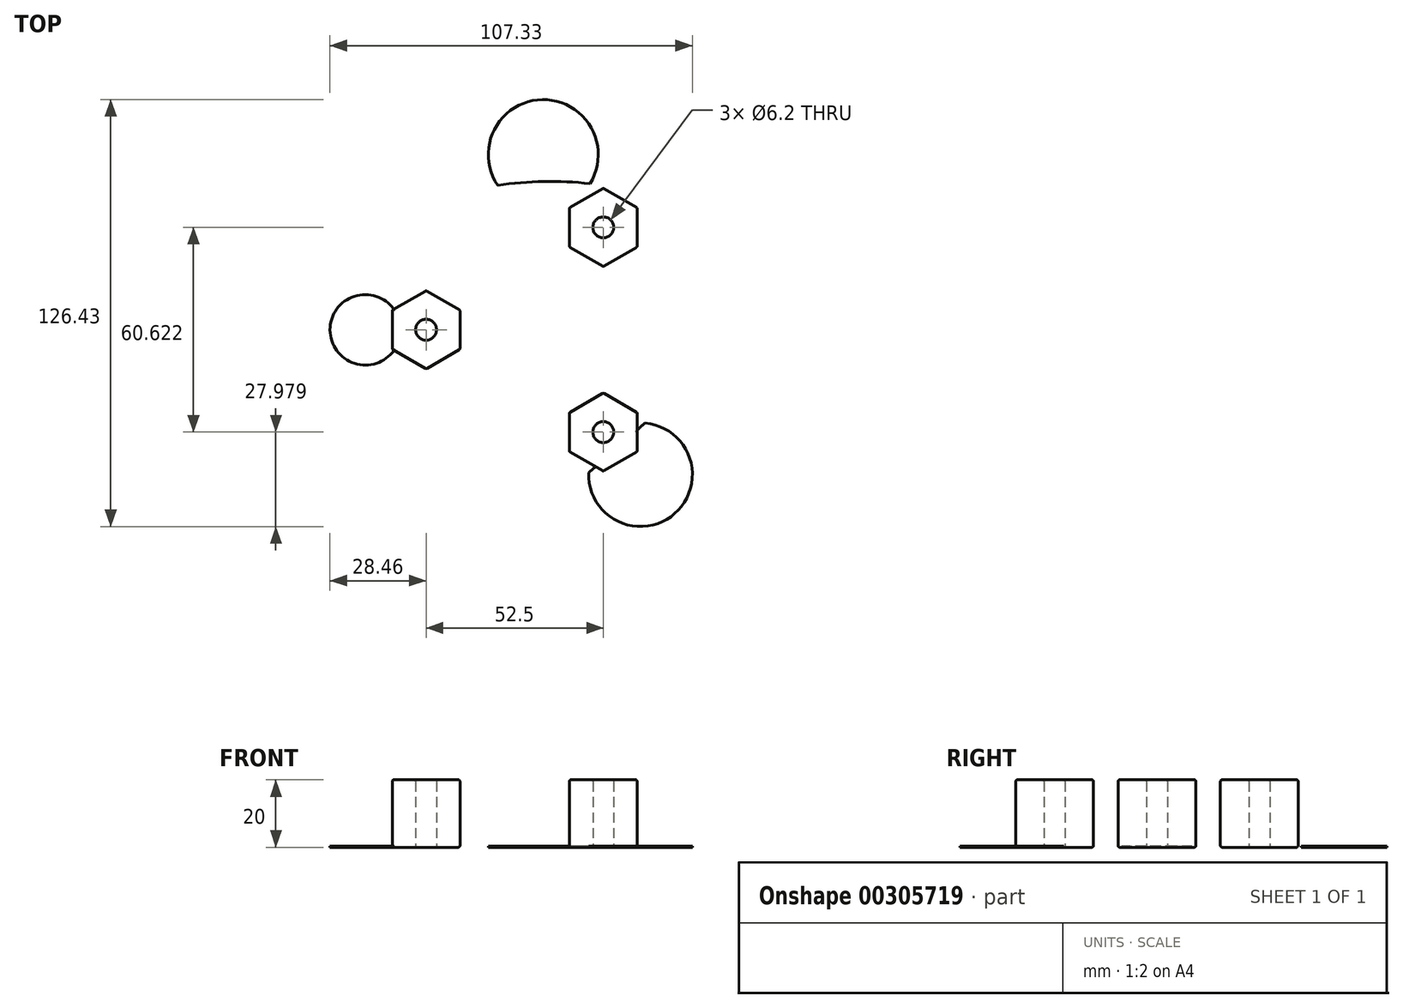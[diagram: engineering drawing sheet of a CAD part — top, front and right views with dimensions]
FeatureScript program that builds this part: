
annotation { "Feature Type Name" : "Feature", "Feature Type Description" : "" }
export const myFeature = defineFeature(function(context is Context, id is Id, definition is map)
    precondition{}
    {
        {
            var Q0;
            Q0=qCreatedBy(makeId("Top.planeOp"),FACE);
            var sketch = newSketch(context, id + "F0", { "sketchPlane" : qUnion([Q0])});
            skCircle(sketch, "E0.cCircle", {"center": v(0, 0) * mm, "radius": 52 * mm, "construction": true});
            skLineSegment(sketch, "E0.0", {"start": v(15, 43.34) * mm, "end": v(27.53, 36.1) * mm});
            skLineSegment(sketch, "E0.2", {"start": v(27.53, -36.1) * mm, "end": v(15, -43.34) * mm});
            skLineSegment(sketch, "E0.4", {"start": v(-45.03, -5.8) * mm, "end": v(-45.03, 5.8) * mm});
            skCircle(sketch, "E1", {"center": v(0, 38) * mm, "radius": 2.1 * mm});
            skCircle(sketch, "E2", {"center": v(0, -38) * mm, "radius": 2.1 * mm});
            skCircle(sketch, "E3.cCircle", {"center": v(0, 0) * mm, "radius": 35 * mm, "construction": true});
            skLineSegment(sketch, "E3.0", {"start": v(-35, 0) * mm, "end": v(-32.32, 1.55) * mm});
            skLineSegment(sketch, "E3.1", {"start": v(17.5, 30.31) * mm, "end": v(17.5, 27.21) * mm});
            skLineSegment(sketch, "E3.2", {"start": v(17.5, -30.31) * mm, "end": v(14.82, -28.76) * mm});
            skCircle(sketch, "E4", {"center": v(17.5, 30.31) * mm, "radius": 3.1 * mm});
            skCircle(sketch, "E5", {"center": v(17.5, -30.31) * mm, "radius": 3.1 * mm});
            skCircle(sketch, "E6", {"center": v(-35, 0) * mm, "radius": 3.1 * mm});
            skLineSegment(sketch, "E7.trimOffspring", {"start": v(14.82, 28.76) * mm, "end": v(17.5, 30.31) * mm});
            skLineSegment(sketch, "E8.trimOffspring", {"start": v(-32.32, -1.55) * mm, "end": v(-35, 0) * mm});
            skLineSegment(sketch, "E9.trimOffspring", {"start": v(17.5, -27.21) * mm, "end": v(17.5, -30.31) * mm});
            skCircle(sketch, "E10.cCircle", {"center": v(17.5, 30.31) * mm, "radius": 5.05 * mm, "construction": true});
            skLineSegment(sketch, "E10.0", {"start": v(17.5, 36.14) * mm, "end": v(22.55, 33.23) * mm});
            skLineSegment(sketch, "E10.1", {"start": v(22.55, 33.23) * mm, "end": v(22.55, 27.4) * mm});
            skLineSegment(sketch, "E10.2", {"start": v(22.55, 27.4) * mm, "end": v(17.5, 24.48) * mm});
            skLineSegment(sketch, "E10.3", {"start": v(17.5, 24.48) * mm, "end": v(12.45, 27.4) * mm});
            skLineSegment(sketch, "E10.4", {"start": v(12.45, 27.4) * mm, "end": v(12.45, 33.23) * mm});
            skLineSegment(sketch, "E10.5", {"start": v(12.45, 33.23) * mm, "end": v(17.5, 36.14) * mm});
            skCircle(sketch, "E11.cCircle", {"center": v(-35, 0) * mm, "radius": 5.05 * mm, "construction": true});
            skLineSegment(sketch, "E11.0", {"start": v(-29.95, 2.92) * mm, "end": v(-29.95, -2.92) * mm});
            skLineSegment(sketch, "E11.1", {"start": v(-29.95, -2.92) * mm, "end": v(-35, -5.83) * mm});
            skLineSegment(sketch, "E11.2", {"start": v(-35, -5.83) * mm, "end": v(-40.05, -2.92) * mm});
            skLineSegment(sketch, "E11.3", {"start": v(-40.05, -2.92) * mm, "end": v(-40.05, 2.92) * mm});
            skLineSegment(sketch, "E11.4", {"start": v(-40.05, 2.92) * mm, "end": v(-35, 5.83) * mm});
            skLineSegment(sketch, "E11.5", {"start": v(-35, 5.83) * mm, "end": v(-29.95, 2.92) * mm});
            skPoint(sketch, "E11.0.midPoint", {"position": v(-29.95, 0) * mm});
            skCircle(sketch, "E12.cCircle", {"center": v(17.5, -30.31) * mm, "radius": 5.05 * mm, "construction": true});
            skLineSegment(sketch, "E12.0", {"start": v(22.55, -33.23) * mm, "end": v(17.5, -36.14) * mm});
            skLineSegment(sketch, "E12.1", {"start": v(17.5, -36.14) * mm, "end": v(12.45, -33.23) * mm});
            skLineSegment(sketch, "E12.2", {"start": v(12.45, -33.23) * mm, "end": v(12.45, -27.4) * mm});
            skLineSegment(sketch, "E12.3", {"start": v(12.45, -27.4) * mm, "end": v(17.5, -24.48) * mm});
            skLineSegment(sketch, "E12.4", {"start": v(17.5, -24.48) * mm, "end": v(22.55, -27.4) * mm});
            skLineSegment(sketch, "E12.5", {"start": v(22.55, -27.4) * mm, "end": v(22.55, -33.23) * mm});
            skPoint(sketch, "E12.0.midPoint", {"position": v(20.02, -34.68) * mm});
            skCircle(sketch, "E13.cCircle", {"center": v(17.5, 30.31) * mm, "radius": 10.03 * mm, "construction": true});
            skLineSegment(sketch, "E13.0", {"start": v(17.5, 41.9) * mm, "end": v(27.53, 36.1) * mm});
            skLineSegment(sketch, "E13.1", {"start": v(27.53, 36.1) * mm, "end": v(27.53, 24.52) * mm});
            skLineSegment(sketch, "E13.2", {"start": v(27.53, 24.52) * mm, "end": v(17.5, 18.73) * mm});
            skLineSegment(sketch, "E13.3", {"start": v(17.5, 18.73) * mm, "end": v(7.47, 24.52) * mm});
            skLineSegment(sketch, "E13.4", {"start": v(7.47, 24.52) * mm, "end": v(7.47, 36.1) * mm});
            skLineSegment(sketch, "E13.5", {"start": v(7.47, 36.1) * mm, "end": v(17.5, 41.9) * mm});
            skCircle(sketch, "E14.cCircle", {"center": v(-35, 0) * mm, "radius": 10.03 * mm, "construction": true});
            skLineSegment(sketch, "E14.1", {"start": v(-45.03, 5.8) * mm, "end": v(-35, 11.59) * mm});
            skLineSegment(sketch, "E14.2", {"start": v(-35, 11.59) * mm, "end": v(-24.97, 5.8) * mm});
            skLineSegment(sketch, "E14.3", {"start": v(-24.97, 5.8) * mm, "end": v(-24.97, -5.8) * mm});
            skLineSegment(sketch, "E14.4", {"start": v(-24.97, -5.8) * mm, "end": v(-35, -11.59) * mm});
            skLineSegment(sketch, "E14.5", {"start": v(-35, -11.59) * mm, "end": v(-45.03, -5.8) * mm});
            skPoint(sketch, "E14.0.midPoint", {"position": v(-45.03, 0) * mm});
            skCircle(sketch, "E15.cCircle", {"center": v(17.5, -30.31) * mm, "radius": 10.03 * mm, "construction": true});
            skLineSegment(sketch, "E15.0", {"start": v(27.53, -36.1) * mm, "end": v(17.5, -41.9) * mm});
            skLineSegment(sketch, "E15.1", {"start": v(17.5, -41.9) * mm, "end": v(7.47, -36.1) * mm});
            skLineSegment(sketch, "E15.2", {"start": v(7.47, -36.1) * mm, "end": v(7.47, -24.52) * mm});
            skLineSegment(sketch, "E15.3", {"start": v(7.47, -24.52) * mm, "end": v(17.5, -18.73) * mm});
            skLineSegment(sketch, "E15.4", {"start": v(17.5, -18.73) * mm, "end": v(27.53, -24.52) * mm});
            skLineSegment(sketch, "E15.5", {"start": v(27.53, -24.52) * mm, "end": v(27.53, -36.1) * mm});
            skPoint(sketch, "E16.endSnap0", {"position": v(45.03, 0) * mm});
            skLineSegment(sketch, "E17", {"start": v(29.5, 10.5) * mm, "end": v(-11.5, 10.5) * mm});
            skLineSegment(sketch, "E18", {"start": v(-11.5, -10.5) * mm, "end": v(29.5, -10.5) * mm});
            skArc(sketch, "E19", {"start": v(-13.17, 3.97) * mm, "mid": v(-15, 7.1) * mm, "end": v(-16.83, 3.97) * mm});
            skArc(sketch, "E20", {"start": v(-16.83, -3.97) * mm, "mid": v(-15, -7.1) * mm, "end": v(-13.17, -3.97) * mm});
            skArc(sketch, "E21", {"start": v(34.83, 3.97) * mm, "mid": v(33.03, 7.1) * mm, "end": v(31.14, 4.02) * mm});
            skArc(sketch, "E22", {"start": v(34.3, -6.97) * mm, "mid": v(35.3, -5.55) * mm, "end": v(35.05, -3.84) * mm});
            skLineSegment(sketch, "E23", {"start": v(9, -10.5) * mm, "end": v(9, 10.5) * mm});
            skPoint(sketch, "E24.visualSharp", {"position": v(31.35, -3.32) * mm});
            skPoint(sketch, "E25.endSnap0", {"position": v(-11.5, 0) * mm});
            skLineSegment(sketch, "E26", {"start": v(-17.5, 0) * mm, "end": v(-17.5, 3.19) * mm});
            skLineSegment(sketch, "E27", {"start": v(-17.19, 3.5) * mm, "end": v(-17.1, 3.5) * mm});
            skLineSegment(sketch, "E28", {"start": v(-12.31, -3.5) * mm, "end": v(-12.9, -3.5) * mm});
            skLineSegment(sketch, "E29", {"start": v(-17.5, -3.19) * mm, "end": v(-17.5, 0) * mm});
            skLineSegment(sketch, "E30.trimOffspring", {"start": v(-12.9, 3.5) * mm, "end": v(-12.31, 3.5) * mm});
            skLineSegment(sketch, "E31.trimOffspring", {"start": v(-17.1, -3.5) * mm, "end": v(-17.19, -3.5) * mm});
            skPoint(sketch, "E25.start.orphan", {"position": v(-11.5, 0) * mm});
            skPoint(sketch, "E32.visualSharp", {"position": v(-13.53, 3.5) * mm});
            skArc(sketch, "E32.filletArc", {"start": v(-13.17, 3.97) * mm, "mid": v(-13.17, 3.65) * mm, "end": v(-12.9, 3.5) * mm});
            skPoint(sketch, "E33.visualSharp", {"position": v(-16.47, 3.5) * mm});
            skArc(sketch, "E33.filletArc", {"start": v(-17.1, 3.5) * mm, "mid": v(-16.83, 3.65) * mm, "end": v(-16.83, 3.97) * mm});
            skPoint(sketch, "E34.visualSharp", {"position": v(-17.5, 3.5) * mm});
            skArc(sketch, "E34.filletArc", {"start": v(-17.19, 3.5) * mm, "mid": v(-17.4, 3.4) * mm, "end": v(-17.5, 3.19) * mm});
            skPoint(sketch, "E35.visualSharp", {"position": v(-16.47, -3.5) * mm});
            skArc(sketch, "E35.filletArc", {"start": v(-16.83, -3.97) * mm, "mid": v(-16.83, -3.65) * mm, "end": v(-17.1, -3.5) * mm});
            skPoint(sketch, "E36.visualSharp", {"position": v(-17.5, -3.5) * mm});
            skArc(sketch, "E36.filletArc", {"start": v(-17.5, -3.19) * mm, "mid": v(-17.4, -3.4) * mm, "end": v(-17.19, -3.5) * mm});
            skPoint(sketch, "E37.visualSharp", {"position": v(-13.53, -3.5) * mm});
            skArc(sketch, "E37.filletArc", {"start": v(-12.9, -3.5) * mm, "mid": v(-13.17, -3.65) * mm, "end": v(-13.17, -3.97) * mm});
            skPoint(sketch, "E38.visualSharp", {"position": v(-11.5, -3.5) * mm});
            skPoint(sketch, "E39.visualSharp", {"position": v(-11.5, 3.5) * mm});
            skArc(sketch, "E40", {"start": v(31.14, 4.02) * mm, "mid": v(32.97, 2.9) * mm, "end": v(34.83, 3.97) * mm});
            skArc(sketch, "E41", {"start": v(35.05, -3.84) * mm, "mid": v(30.7, -4.45) * mm, "end": v(34.3, -6.97) * mm});
            skLineSegment(sketch, "E42.bottom", {"start": v(29.5, 10.5) * mm, "end": v(30, 10.5) * mm});
            skLineSegment(sketch, "E42.top", {"start": v(29.5, -10.5) * mm, "end": v(30, -10.5) * mm});
            skLineSegment(sketch, "E42.right", {"start": v(30, 10.5) * mm, "end": v(30, -10.5) * mm});
            skLineSegment(sketch, "E43.bottom", {"start": v(-11.5, 10.5) * mm, "end": v(-12, 10.5) * mm});
            skLineSegment(sketch, "E43.right", {"start": v(-12, 10.5) * mm, "end": v(-12, 3.81) * mm});
            skLineSegment(sketch, "E44.bottom", {"start": v(-11.5, -10.5) * mm, "end": v(-12, -10.5) * mm});
            skLineSegment(sketch, "E44.right", {"start": v(-12, -10.5) * mm, "end": v(-12, -3.81) * mm});
            skPoint(sketch, "E45.visualSharp", {"position": v(-12, -3.5) * mm});
            skArc(sketch, "E45.filletArc", {"start": v(-12, -3.81) * mm, "mid": v(-12.1, -3.6) * mm, "end": v(-12.31, -3.5) * mm});
            skPoint(sketch, "E46.visualSharp", {"position": v(-12, 3.5) * mm});
            skArc(sketch, "E46.filletArc", {"start": v(-12.31, 3.5) * mm, "mid": v(-12.1, 3.6) * mm, "end": v(-12, 3.81) * mm});
            skPoint(sketch, "E47.visualSharp", {"position": v(0, 52) * mm});
            skArc(sketch, "E47.filletArc", {"start": v(15, 43.34) * mm, "mid": v(0, 47.36) * mm, "end": v(-15, 43.34) * mm});
            skPoint(sketch, "E48.visualSharp", {"position": v(-45.03, 26) * mm});
            skPoint(sketch, "E49.visualSharp", {"position": v(45.03, 26) * mm});
            skPoint(sketch, "E50.visualSharp", {"position": v(45.03, -26) * mm});
            skPoint(sketch, "E51.visualSharp", {"position": v(0, -52) * mm});
            skArc(sketch, "E51.filletArc", {"start": v(-15, -43.34) * mm, "mid": v(0, -47.36) * mm, "end": v(15, -43.34) * mm});
            skPoint(sketch, "E52.visualSharp", {"position": v(-45.03, -26) * mm});
            skArc(sketch, "E53", {"start": v(-35, 11.59) * mm, "mid": v(-21.07, 24.99) * mm, "end": v(-15, 43.34) * mm});
            skArc(sketch, "E54", {"start": v(-15, -43.34) * mm, "mid": v(-21.07, -24.99) * mm, "end": v(-35, -11.59) * mm});
            skArc(sketch, "E55", {"start": v(27.53, -36.1) * mm, "mid": v(40.6, 0) * mm, "end": v(27.53, 36.1) * mm});
            skSolve(sketch);
        }
        {
            var Q0;
            Q0=makeQuery(id+"F0.imprint","IMPRINT",FACE,{"disambiguationData":[TD([[makeQuery(id+"F0.imprint","IMPRINT",EDGE,{"derivedFrom":sQuery(id+"F0.wireOp",EDGE,"E10.0")}),1.0]])]});
            var Q1;
            Q1=makeQuery(id+"F0.imprint","IMPRINT",FACE,{"disambiguationData":[TD([[makeQuery(id+"F0.imprint","IMPRINT",EDGE,{"derivedFrom":sQuery(id+"F0.wireOp",EDGE,"E0.0")}),-1.0]])]});
            var Q2;
            Q2=makeQuery(id+"F0.imprint","IMPRINT",FACE,{"disambiguationData":[TD([[makeQuery(id+"F0.imprint","IMPRINT",EDGE,{"derivedFrom":sQuery(id+"F0.wireOp",EDGE,"E12.0")}),1.0]])]});
            var Q3;
            Q3=makeQuery(id+"F0.imprint","IMPRINT",FACE,{"disambiguationData":[TD([[makeQuery(id+"F0.imprint","IMPRINT",EDGE,{"derivedFrom":sQuery(id+"F0.wireOp",EDGE,"E11.0")}),1.0]])]});
            var Q4;
            Q4=makeQuery(id+"F0.imprint","IMPRINT",FACE,{"disambiguationData":[TD([[makeQuery(id+"F0.imprint","IMPRINT",EDGE,{"derivedFrom":sQuery(id+"F0.wireOp",EDGE,"E11.0")}),-1.0]])]});
            var Q5;
            Q5=makeQuery(id+"F0.imprint","IMPRINT",FACE,{"disambiguationData":[TD([[makeQuery(id+"F0.imprint","IMPRINT",EDGE,{"derivedFrom":sQuery(id+"F0.wireOp",EDGE,"E10.0")}),-1.0]])]});
            var Q6;
            Q6=makeQuery(id+"F0.imprint","IMPRINT",FACE,{"disambiguationData":[TD([[makeQuery(id+"F0.imprint","IMPRINT",EDGE,{"derivedFrom":sQuery(id+"F0.wireOp",EDGE,"E12.0")}),-1.0]])]});
            extrude(context, id + "F1", {"entities" : qUnion([Q0, Q1, Q2, Q3, Q4, Q5, Q6]), "depth" : 5 * mm});
        }
        {
            var Q0;
            Q0=makeQuery(id+"F0.imprint","IMPRINT",FACE,{"disambiguationData":[TD([[makeQuery(id+"F0.imprint","IMPRINT",EDGE,{"derivedFrom":sQuery(id+"F0.wireOp",EDGE,"E12.0")}),1.0]])]});
            var Q1;
            Q1=makeQuery(id+"F0.imprint","IMPRINT",FACE,{"disambiguationData":[TD([[makeQuery(id+"F0.imprint","IMPRINT",EDGE,{"derivedFrom":sQuery(id+"F0.wireOp",EDGE,"E10.0")}),1.0]])]});
            var Q2;
            Q2=makeQuery(id+"F0.imprint","IMPRINT",FACE,{"disambiguationData":[TD([[makeQuery(id+"F0.imprint","IMPRINT",EDGE,{"derivedFrom":sQuery(id+"F0.wireOp",EDGE,"E12.0")}),-1.0]])]});
            var Q3;
            Q3=makeQuery(id+"F0.imprint","IMPRINT",FACE,{"disambiguationData":[TD([[makeQuery(id+"F0.imprint","IMPRINT",EDGE,{"derivedFrom":sQuery(id+"F0.wireOp",EDGE,"E10.0")}),-1.0]])]});
            var Q4;
            Q4=makeQuery(id+"F0.imprint","IMPRINT",FACE,{"disambiguationData":[TD([[makeQuery(id+"F0.imprint","IMPRINT",EDGE,{"derivedFrom":sQuery(id+"F0.wireOp",EDGE,"E11.0")}),-1.0]])]});
            var Q5;
            Q5=makeQuery(id+"F0.imprint","IMPRINT",FACE,{"disambiguationData":[TD([[makeQuery(id+"F0.imprint","IMPRINT",EDGE,{"derivedFrom":sQuery(id+"F0.wireOp",EDGE,"E11.0")}),1.0]])]});
            extrude(context, id + "F2", {"entities" : qUnion([Q0, Q1, Q2, Q3, Q4, Q5]), "operationType" : NewBodyOperationType.ADD, "depth" : 20 * mm});
        }
        {
            var Q0;
            {var subQ0=sQuery(id+"F0.wireOp",EDGE,"E13.0");Q0=makeQuery(id+"F2.boolean.opBoolean","MERGE",FACE,{"derivedFrom":[makeQuery(id+"F1.opExtrude","SWEPT_FACE",FACE,{"disambiguationData":[OSD([sQuery(id+"F0.wireOp",EDGE,"E0.0"),subQ0])]}),makeQuery(id+"F2.opExtrude","SWEPT_FACE",FACE,{"disambiguationData":[OSD([subQ0])]})]});}
            var Q1;
            {var subQ0=sQuery(id+"F0.wireOp",EDGE,"E0.4");Q1=makeQuery(id+"F2.boolean.opBoolean","MERGE",FACE,{"derivedFrom":[makeQuery(id+"F1.opExtrude","SWEPT_FACE",FACE,{"disambiguationData":[OSD([sQuery(id+"F0.wireOp",EDGE,"E0.4"),subQ0])]}),makeQuery(id+"F2.opExtrude","SWEPT_FACE",FACE,{"disambiguationData":[OSD([subQ0])]})]});}
            var Q2;
            Q2=makeQuery(id+"F2.opExtrude","SWEPT_EDGE",EDGE,{"disambiguationData":[OSD([sQuery(id+"F0.wireOp",EDGE,"E13.1"),sQuery(id+"F0.wireOp",EDGE,"E13.2")])]});
            var Q3;
            Q3=makeQuery(id+"F2.opExtrude","CAP_EDGE",EDGE,{"disambiguationData":[OSD([sQuery(id+"F0.wireOp",EDGE,"E13.2")])],"isStart":false});
            var Q4;
            Q4=makeQuery(id+"F2.opExtrude","SWEPT_EDGE",EDGE,{"disambiguationData":[OSD([sQuery(id+"F0.wireOp",EDGE,"E0.4"),sQuery(id+"F0.wireOp",EDGE,"E0.4"),sQuery(id+"F0.wireOp",EDGE,"E14.5")])]});
            var Q5;
            Q5=makeQuery(id+"F1.opExtrude","CAP_EDGE",EDGE,{"disambiguationData":[OSD([sQuery(id+"F0.wireOp",EDGE,"E0.1")])],"isStart":false});
            var Q6;
            {var subQ0=sQuery(id+"F0.wireOp",EDGE,"E0.5");var subQ1=sQuery(id+"F0.wireOp",EDGE,"E0.4");var subQ2=sQuery(id+"F0.wireOp",EDGE,"E0.4");Q6=makeQuery(id+"F2.boolean.opBoolean","SPLIT",EDGE,{"disambiguationData":[TD([makeQuery(id+"F1.opExtrude","SWEPT_FACE",FACE,{"disambiguationData":[OSD([subQ0])]})])],"derivedFrom":makeQuery(id+"F1.opExtrude","CAP_EDGE",EDGE,{"disambiguationData":[OSD([subQ2,subQ1])],"isStart":false})});}
            var Q7;
            Q7=makeQuery(id+"F2.opExtrude","SWEPT_FACE",FACE,{"disambiguationData":[OSD([sQuery(id+"F0.wireOp",EDGE,"E14.3")])]});
            var Q8;
            Q8=makeQuery(id+"F2.opExtrude","SWEPT_FACE",FACE,{"disambiguationData":[OSD([sQuery(id+"F0.wireOp",EDGE,"E14.1")])]});
            var Q9;
            Q9=makeQuery(id+"F2.opExtrude","CAP_EDGE",EDGE,{"disambiguationData":[OSD([sQuery(id+"F0.wireOp",EDGE,"E14.2")])],"isStart":false});
            var Q10;
            Q10=makeQuery(id+"F2.opExtrude","SWEPT_FACE",FACE,{"disambiguationData":[OSD([sQuery(id+"F0.wireOp",EDGE,"E15.2")])]});
            var Q11;
            Q11=makeQuery(id+"F2.opExtrude","CAP_EDGE",EDGE,{"disambiguationData":[OSD([sQuery(id+"F0.wireOp",EDGE,"E14.3")])],"isStart":false});
            var Q12;
            Q12=makeQuery(id+"F2.opExtrude","SWEPT_EDGE",EDGE,{"disambiguationData":[OSD([sQuery(id+"F0.wireOp",EDGE,"E14.3"),sQuery(id+"F0.wireOp",EDGE,"E14.4")])]});
            var Q13;
            Q13=makeQuery(id+"F1.opExtrude","CAP_EDGE",EDGE,{"disambiguationData":[OSD([sQuery(id+"F0.wireOp",EDGE,"E18")])],"isStart":false});
            var Q14;
            {var subQ0=sQuery(id+"F0.wireOp",EDGE,"E15.0");Q14=makeQuery(id+"F2.boolean.opBoolean","MERGE",FACE,{"derivedFrom":[makeQuery(id+"F1.opExtrude","SWEPT_FACE",FACE,{"disambiguationData":[OSD([sQuery(id+"F0.wireOp",EDGE,"E0.2"),subQ0])]}),makeQuery(id+"F2.opExtrude","SWEPT_FACE",FACE,{"disambiguationData":[OSD([subQ0])]})]});}
            var Q15;
            Q15=makeQuery(id+"F2.opExtrude","CAP_EDGE",EDGE,{"disambiguationData":[OSD([sQuery(id+"F0.wireOp",EDGE,"E15.5")])],"isStart":false});
            var Q16;
            Q16=makeQuery(id+"F2.opExtrude","CAP_FACE",FACE,{"disambiguationData":[OSD([sQuery(id+"F0.wireOp",EDGE,"E4"),sQuery(id+"F0.wireOp",EDGE,"E13.0"),sQuery(id+"F0.wireOp",EDGE,"E13.1"),sQuery(id+"F0.wireOp",EDGE,"E13.2"),sQuery(id+"F0.wireOp",EDGE,"E13.3"),sQuery(id+"F0.wireOp",EDGE,"E13.4"),sQuery(id+"F0.wireOp",EDGE,"E13.5")])],"isStart":false});
            var Q17;
            Q17=makeQuery(id+"F2.opExtrude","SWEPT_EDGE",EDGE,{"disambiguationData":[OSD([sQuery(id+"F0.wireOp",EDGE,"E15.2"),sQuery(id+"F0.wireOp",EDGE,"E15.3")])]});
            var Q18;
            {var subQ0=sQuery(id+"F0.wireOp",EDGE,"E5");Q18=makeQuery(id+"F2.boolean.opBoolean","MERGE",FACE,{"derivedFrom":[makeQuery(id+"F1.opExtrude","SWEPT_FACE",FACE,{"disambiguationData":[OSD([subQ0])]}),makeQuery(id+"F2.opExtrude","SWEPT_FACE",FACE,{"disambiguationData":[OSD([subQ0])]})]});}
            var Q19;
            Q19=makeQuery(id+"F2.opExtrude","CAP_EDGE",EDGE,{"disambiguationData":[OSD([sQuery(id+"F0.wireOp",EDGE,"E14.5")])],"isStart":false});
            var Q20;
            Q20=makeQuery(id+"F2.opExtrude","SWEPT_FACE",FACE,{"disambiguationData":[OSD([sQuery(id+"F0.wireOp",EDGE,"E13.3")])]});
            var Q21;
            {var subQ0=sQuery(id+"F0.wireOp",EDGE,"E13.0");var subQ1=sQuery(id+"F0.wireOp",EDGE,"E0.0");var subQ2=sQuery(id+"F0.wireOp",EDGE,"E0.1");Q21=makeQuery(id+"F2.boolean.opBoolean","SPLIT",EDGE,{"disambiguationData":[TD([makeQuery(id+"F1.opExtrude","SWEPT_FACE",FACE,{"disambiguationData":[OSD([subQ2])]})])],"derivedFrom":makeQuery(id+"F1.opExtrude","CAP_EDGE",EDGE,{"disambiguationData":[OSD([subQ1,subQ0])],"isStart":false})});}
            var Q22;
            Q22=makeQuery(id+"F2.opExtrude","CAP_EDGE",EDGE,{"disambiguationData":[OSD([sQuery(id+"F0.wireOp",EDGE,"E0.4")])],"isStart":false});
            var Q23;
            Q23=makeQuery(id+"F1.opExtrude","SWEPT_FACE",FACE,{"disambiguationData":[OSD([sQuery(id+"F0.wireOp",EDGE,"E0.5")])]});
            var Q24;
            Q24=makeQuery(id+"F2.opExtrude","SWEPT_FACE",FACE,{"disambiguationData":[OSD([sQuery(id+"F0.wireOp",EDGE,"E15.5")])]});
            var Q25;
            Q25=makeQuery(id+"F2.opExtrude","SWEPT_FACE",FACE,{"disambiguationData":[OSD([sQuery(id+"F0.wireOp",EDGE,"E13.2")])]});
            var Q26;
            Q26=makeQuery(id+"F2.opExtrude","CAP_EDGE",EDGE,{"disambiguationData":[OSD([sQuery(id+"F0.wireOp",EDGE,"E13.5")])],"isStart":false});
            var Q27;
            Q27=makeQuery(id+"F2.opExtrude","SWEPT_FACE",FACE,{"disambiguationData":[OSD([sQuery(id+"F0.wireOp",EDGE,"E13.1")])]});
            var Q28;
            Q28=makeQuery(id+"F2.opExtrude","CAP_EDGE",EDGE,{"disambiguationData":[OSD([sQuery(id+"F0.wireOp",EDGE,"E13.3")])],"isStart":false});
            var Q29;
            Q29=makeQuery(id+"F2.boolean.opBoolean","INTERSECT",EDGE,{"derivedFrom":[makeQuery(id+"F1.opExtrude","CAP_FACE",FACE,{"disambiguationData":[OSD([sQuery(id+"F0.wireOp",EDGE,"E0.0"),sQuery(id+"F0.wireOp",EDGE,"E0.1"),sQuery(id+"F0.wireOp",EDGE,"E0.2"),sQuery(id+"F0.wireOp",EDGE,"E0.3"),sQuery(id+"F0.wireOp",EDGE,"E0.4"),sQuery(id+"F0.wireOp",EDGE,"E0.5"),sQuery(id+"F0.wireOp",EDGE,"E1"),sQuery(id+"F0.wireOp",EDGE,"E2"),sQuery(id+"F0.wireOp",EDGE,"E4"),sQuery(id+"F0.wireOp",EDGE,"E5"),sQuery(id+"F0.wireOp",EDGE,"E6"),sQuery(id+"F0.wireOp",EDGE,"E13.0"),sQuery(id+"F0.wireOp",EDGE,"E0.4"),sQuery(id+"F0.wireOp",EDGE,"E15.0"),sQuery(id+"F0.wireOp",EDGE,"W6VNMVPK-Heu4-H590-lQcW-GhW6zsYcIm86"),sQuery(id+"F0.wireOp",EDGE,"E17"),sQuery(id+"F0.wireOp",EDGE,"kWYB9zZw-dUfE-JBuI-mU9n-pgfyDcaRUxvO"),sQuery(id+"F0.wireOp",EDGE,"E18"),sQuery(id+"F0.wireOp",EDGE,"vfnI13aN-5aGC-TwJ9-h9OO-FMGUWFeDmuv9"),sQuery(id+"F0.wireOp",EDGE,"E19"),sQuery(id+"F0.wireOp",EDGE,"E20"),sQuery(id+"F0.wireOp",EDGE,"E21"),sQuery(id+"F0.wireOp",EDGE,"E22"),sQuery(id+"F0.wireOp",EDGE,"JsAoEpAL-XQW4-Lyrg-R8HR-OfjOjkPQAlpN"),sQuery(id+"F0.wireOp",EDGE,"QAwi9ICx-SNt3-gAxD-qMH3-k1r5QHOYkTIN"),sQuery(id+"F0.wireOp",EDGE,"bgABXGzA-3ZDr-4HFO-1yYm-MuwqDgoMTBvo"),sQuery(id+"F0.wireOp",EDGE,"wgyuN0RA-UE8u-KT4Y-o13n-P3vcXdWd7IlJ"),sQuery(id+"F0.wireOp",EDGE,"9d0d2092-a8f3-4ebb-af6d-0df3fb4feacb.trimOffspring"),sQuery(id+"F0.wireOp",EDGE,"10fe8deb-c225-4385-8b94-fba867b40c2d.trimOffspring"),sQuery(id+"F0.wireOp",EDGE,"75751931-a2df-4963-a2bf-7204bff7b78a.filletArc"),sQuery(id+"F0.wireOp",EDGE,"e7d6d30a-f864-4f75-85fc-35ceeb29439c.filletArc"),sQuery(id+"F0.wireOp",EDGE,"a49e830f-b283-406d-92e2-e5d81fe63434.filletArc"),sQuery(id+"F0.wireOp",EDGE,"b3d7f47c-b04d-42dd-9b78-bc98ec63f042.filletArc"),sQuery(id+"F0.wireOp",EDGE,"b51091e8-612c-49d7-9d92-63615423fc4d.filletArc"),sQuery(id+"F0.wireOp",EDGE,"E24.filletArc")])],"isStart":false}),makeQuery(id+"F2.opExtrude","SWEPT_FACE",FACE,{"disambiguationData":[OSD([sQuery(id+"F0.wireOp",EDGE,"E15.2")])]})]});
            var Q30;
            Q30=makeQuery(id+"F2.opExtrude","SWEPT_FACE",FACE,{"disambiguationData":[OSD([sQuery(id+"F0.wireOp",EDGE,"E15.1")])]});
            var Q31;
            Q31=makeQuery(id+"F1.opExtrude","SWEPT_FACE",FACE,{"disambiguationData":[OSD([sQuery(id+"F0.wireOp",EDGE,"E0.1")])]});
            var Q32;
            Q32=makeQuery(id+"F2.opExtrude","SWEPT_EDGE",EDGE,{"disambiguationData":[OSD([sQuery(id+"F0.wireOp",EDGE,"E14.4"),sQuery(id+"F0.wireOp",EDGE,"E14.5")])]});
            var Q33;
            Q33=makeQuery(id+"F2.opExtrude","SWEPT_EDGE",EDGE,{"disambiguationData":[OSD([sQuery(id+"F0.wireOp",EDGE,"E13.4"),sQuery(id+"F0.wireOp",EDGE,"E13.5")])]});
            var Q34;
            Q34=makeQuery(id+"F2.opExtrude","CAP_FACE",FACE,{"disambiguationData":[OSD([sQuery(id+"F0.wireOp",EDGE,"E6"),sQuery(id+"F0.wireOp",EDGE,"E0.4"),sQuery(id+"F0.wireOp",EDGE,"E14.1"),sQuery(id+"F0.wireOp",EDGE,"E14.2"),sQuery(id+"F0.wireOp",EDGE,"E14.3"),sQuery(id+"F0.wireOp",EDGE,"E14.4"),sQuery(id+"F0.wireOp",EDGE,"E14.5")])],"isStart":false});
            var Q35;
            Q35=makeQuery(id+"F2.opExtrude","SWEPT_FACE",FACE,{"disambiguationData":[OSD([sQuery(id+"F0.wireOp",EDGE,"E14.5")])]});
            var Q36;
            Q36=makeQuery(id+"F2.opExtrude","CAP_FACE",FACE,{"disambiguationData":[OSD([sQuery(id+"F0.wireOp",EDGE,"E5"),sQuery(id+"F0.wireOp",EDGE,"E15.0"),sQuery(id+"F0.wireOp",EDGE,"E15.1"),sQuery(id+"F0.wireOp",EDGE,"E15.2"),sQuery(id+"F0.wireOp",EDGE,"E15.3"),sQuery(id+"F0.wireOp",EDGE,"E15.4"),sQuery(id+"F0.wireOp",EDGE,"E15.5")])],"isStart":false});
            var Q37;
            Q37=makeQuery(id+"F1.opExtrude","SWEPT_FACE",FACE,{"disambiguationData":[OSD([sQuery(id+"F0.wireOp",EDGE,"E2")])]});
            var Q38;
            Q38=makeQuery(id+"F2.opExtrude","SWEPT_EDGE",EDGE,{"disambiguationData":[OSD([sQuery(id+"F0.wireOp",EDGE,"E0.4"),sQuery(id+"F0.wireOp",EDGE,"E0.4"),sQuery(id+"F0.wireOp",EDGE,"E14.1")])]});
            var Q39;
            Q39=makeQuery(id+"F2.opExtrude","CAP_EDGE",EDGE,{"disambiguationData":[OSD([sQuery(id+"F0.wireOp",EDGE,"E15.2")])],"isStart":false});
            var Q40;
            Q40=makeQuery(id+"F1.opExtrude","CAP_FACE",FACE,{"disambiguationData":[OSD([sQuery(id+"F0.wireOp",EDGE,"E0.0"),sQuery(id+"F0.wireOp",EDGE,"E0.1"),sQuery(id+"F0.wireOp",EDGE,"E0.2"),sQuery(id+"F0.wireOp",EDGE,"E0.3"),sQuery(id+"F0.wireOp",EDGE,"E0.4"),sQuery(id+"F0.wireOp",EDGE,"E0.5"),sQuery(id+"F0.wireOp",EDGE,"E1"),sQuery(id+"F0.wireOp",EDGE,"E2"),sQuery(id+"F0.wireOp",EDGE,"E4"),sQuery(id+"F0.wireOp",EDGE,"E5"),sQuery(id+"F0.wireOp",EDGE,"E6"),sQuery(id+"F0.wireOp",EDGE,"E13.0"),sQuery(id+"F0.wireOp",EDGE,"E0.4"),sQuery(id+"F0.wireOp",EDGE,"E15.0"),sQuery(id+"F0.wireOp",EDGE,"W6VNMVPK-Heu4-H590-lQcW-GhW6zsYcIm86"),sQuery(id+"F0.wireOp",EDGE,"E17"),sQuery(id+"F0.wireOp",EDGE,"kWYB9zZw-dUfE-JBuI-mU9n-pgfyDcaRUxvO"),sQuery(id+"F0.wireOp",EDGE,"E18"),sQuery(id+"F0.wireOp",EDGE,"vfnI13aN-5aGC-TwJ9-h9OO-FMGUWFeDmuv9"),sQuery(id+"F0.wireOp",EDGE,"E19"),sQuery(id+"F0.wireOp",EDGE,"E20"),sQuery(id+"F0.wireOp",EDGE,"E21"),sQuery(id+"F0.wireOp",EDGE,"E22"),sQuery(id+"F0.wireOp",EDGE,"JsAoEpAL-XQW4-Lyrg-R8HR-OfjOjkPQAlpN"),sQuery(id+"F0.wireOp",EDGE,"QAwi9ICx-SNt3-gAxD-qMH3-k1r5QHOYkTIN"),sQuery(id+"F0.wireOp",EDGE,"bgABXGzA-3ZDr-4HFO-1yYm-MuwqDgoMTBvo"),sQuery(id+"F0.wireOp",EDGE,"wgyuN0RA-UE8u-KT4Y-o13n-P3vcXdWd7IlJ"),sQuery(id+"F0.wireOp",EDGE,"9d0d2092-a8f3-4ebb-af6d-0df3fb4feacb.trimOffspring"),sQuery(id+"F0.wireOp",EDGE,"10fe8deb-c225-4385-8b94-fba867b40c2d.trimOffspring"),sQuery(id+"F0.wireOp",EDGE,"75751931-a2df-4963-a2bf-7204bff7b78a.filletArc"),sQuery(id+"F0.wireOp",EDGE,"e7d6d30a-f864-4f75-85fc-35ceeb29439c.filletArc"),sQuery(id+"F0.wireOp",EDGE,"a49e830f-b283-406d-92e2-e5d81fe63434.filletArc"),sQuery(id+"F0.wireOp",EDGE,"b3d7f47c-b04d-42dd-9b78-bc98ec63f042.filletArc"),sQuery(id+"F0.wireOp",EDGE,"b51091e8-612c-49d7-9d92-63615423fc4d.filletArc"),sQuery(id+"F0.wireOp",EDGE,"E24.filletArc")])],"isStart":true});
            var Q41;
            Q41=makeQuery(id+"F1.opExtrude","CAP_EDGE",EDGE,{"disambiguationData":[OSD([sQuery(id+"F0.wireOp",EDGE,"E17")])],"isStart":false});
            var Q42;
            Q42=makeQuery(id+"F1.opExtrude","SWEPT_FACE",FACE,{"disambiguationData":[OSD([sQuery(id+"F0.wireOp",EDGE,"E0.3")])]});
            var Q43;
            Q43=makeQuery(id+"F2.boolean.opBoolean","INTERSECT",EDGE,{"derivedFrom":[makeQuery(id+"F1.opExtrude","CAP_FACE",FACE,{"disambiguationData":[OSD([sQuery(id+"F0.wireOp",EDGE,"E0.0"),sQuery(id+"F0.wireOp",EDGE,"E0.1"),sQuery(id+"F0.wireOp",EDGE,"E0.2"),sQuery(id+"F0.wireOp",EDGE,"E0.3"),sQuery(id+"F0.wireOp",EDGE,"E0.4"),sQuery(id+"F0.wireOp",EDGE,"E0.5"),sQuery(id+"F0.wireOp",EDGE,"E1"),sQuery(id+"F0.wireOp",EDGE,"E2"),sQuery(id+"F0.wireOp",EDGE,"E4"),sQuery(id+"F0.wireOp",EDGE,"E5"),sQuery(id+"F0.wireOp",EDGE,"E6"),sQuery(id+"F0.wireOp",EDGE,"E13.0"),sQuery(id+"F0.wireOp",EDGE,"E0.4"),sQuery(id+"F0.wireOp",EDGE,"E15.0"),sQuery(id+"F0.wireOp",EDGE,"W6VNMVPK-Heu4-H590-lQcW-GhW6zsYcIm86"),sQuery(id+"F0.wireOp",EDGE,"E17"),sQuery(id+"F0.wireOp",EDGE,"kWYB9zZw-dUfE-JBuI-mU9n-pgfyDcaRUxvO"),sQuery(id+"F0.wireOp",EDGE,"E18"),sQuery(id+"F0.wireOp",EDGE,"vfnI13aN-5aGC-TwJ9-h9OO-FMGUWFeDmuv9"),sQuery(id+"F0.wireOp",EDGE,"E19"),sQuery(id+"F0.wireOp",EDGE,"E20"),sQuery(id+"F0.wireOp",EDGE,"E21"),sQuery(id+"F0.wireOp",EDGE,"E22"),sQuery(id+"F0.wireOp",EDGE,"JsAoEpAL-XQW4-Lyrg-R8HR-OfjOjkPQAlpN"),sQuery(id+"F0.wireOp",EDGE,"QAwi9ICx-SNt3-gAxD-qMH3-k1r5QHOYkTIN"),sQuery(id+"F0.wireOp",EDGE,"bgABXGzA-3ZDr-4HFO-1yYm-MuwqDgoMTBvo"),sQuery(id+"F0.wireOp",EDGE,"wgyuN0RA-UE8u-KT4Y-o13n-P3vcXdWd7IlJ"),sQuery(id+"F0.wireOp",EDGE,"9d0d2092-a8f3-4ebb-af6d-0df3fb4feacb.trimOffspring"),sQuery(id+"F0.wireOp",EDGE,"10fe8deb-c225-4385-8b94-fba867b40c2d.trimOffspring"),sQuery(id+"F0.wireOp",EDGE,"75751931-a2df-4963-a2bf-7204bff7b78a.filletArc"),sQuery(id+"F0.wireOp",EDGE,"e7d6d30a-f864-4f75-85fc-35ceeb29439c.filletArc"),sQuery(id+"F0.wireOp",EDGE,"a49e830f-b283-406d-92e2-e5d81fe63434.filletArc"),sQuery(id+"F0.wireOp",EDGE,"b3d7f47c-b04d-42dd-9b78-bc98ec63f042.filletArc"),sQuery(id+"F0.wireOp",EDGE,"b51091e8-612c-49d7-9d92-63615423fc4d.filletArc"),sQuery(id+"F0.wireOp",EDGE,"E24.filletArc")])],"isStart":false}),makeQuery(id+"F2.opExtrude","SWEPT_FACE",FACE,{"disambiguationData":[OSD([sQuery(id+"F0.wireOp",EDGE,"E13.2")])]})]});
            var Q44;
            Q44=makeQuery(id+"F1.opExtrude","CAP_FACE",FACE,{"disambiguationData":[OSD([sQuery(id+"F0.wireOp",EDGE,"E0.0"),sQuery(id+"F0.wireOp",EDGE,"E0.1"),sQuery(id+"F0.wireOp",EDGE,"E0.2"),sQuery(id+"F0.wireOp",EDGE,"E0.3"),sQuery(id+"F0.wireOp",EDGE,"E0.4"),sQuery(id+"F0.wireOp",EDGE,"E0.5"),sQuery(id+"F0.wireOp",EDGE,"E1"),sQuery(id+"F0.wireOp",EDGE,"E2"),sQuery(id+"F0.wireOp",EDGE,"E4"),sQuery(id+"F0.wireOp",EDGE,"E5"),sQuery(id+"F0.wireOp",EDGE,"E6"),sQuery(id+"F0.wireOp",EDGE,"E13.0"),sQuery(id+"F0.wireOp",EDGE,"E0.4"),sQuery(id+"F0.wireOp",EDGE,"E15.0"),sQuery(id+"F0.wireOp",EDGE,"W6VNMVPK-Heu4-H590-lQcW-GhW6zsYcIm86"),sQuery(id+"F0.wireOp",EDGE,"E17"),sQuery(id+"F0.wireOp",EDGE,"kWYB9zZw-dUfE-JBuI-mU9n-pgfyDcaRUxvO"),sQuery(id+"F0.wireOp",EDGE,"E18"),sQuery(id+"F0.wireOp",EDGE,"vfnI13aN-5aGC-TwJ9-h9OO-FMGUWFeDmuv9"),sQuery(id+"F0.wireOp",EDGE,"E19"),sQuery(id+"F0.wireOp",EDGE,"E20"),sQuery(id+"F0.wireOp",EDGE,"E21"),sQuery(id+"F0.wireOp",EDGE,"E22"),sQuery(id+"F0.wireOp",EDGE,"JsAoEpAL-XQW4-Lyrg-R8HR-OfjOjkPQAlpN"),sQuery(id+"F0.wireOp",EDGE,"QAwi9ICx-SNt3-gAxD-qMH3-k1r5QHOYkTIN"),sQuery(id+"F0.wireOp",EDGE,"bgABXGzA-3ZDr-4HFO-1yYm-MuwqDgoMTBvo"),sQuery(id+"F0.wireOp",EDGE,"wgyuN0RA-UE8u-KT4Y-o13n-P3vcXdWd7IlJ"),sQuery(id+"F0.wireOp",EDGE,"9d0d2092-a8f3-4ebb-af6d-0df3fb4feacb.trimOffspring"),sQuery(id+"F0.wireOp",EDGE,"10fe8deb-c225-4385-8b94-fba867b40c2d.trimOffspring"),sQuery(id+"F0.wireOp",EDGE,"75751931-a2df-4963-a2bf-7204bff7b78a.filletArc"),sQuery(id+"F0.wireOp",EDGE,"e7d6d30a-f864-4f75-85fc-35ceeb29439c.filletArc"),sQuery(id+"F0.wireOp",EDGE,"a49e830f-b283-406d-92e2-e5d81fe63434.filletArc"),sQuery(id+"F0.wireOp",EDGE,"b3d7f47c-b04d-42dd-9b78-bc98ec63f042.filletArc"),sQuery(id+"F0.wireOp",EDGE,"b51091e8-612c-49d7-9d92-63615423fc4d.filletArc"),sQuery(id+"F0.wireOp",EDGE,"E24.filletArc")])],"isStart":false});
            var Q45;
            Q45=makeQuery(id+"F2.opExtrude","SWEPT_EDGE",EDGE,{"disambiguationData":[OSD([sQuery(id+"F0.wireOp",EDGE,"E13.3"),sQuery(id+"F0.wireOp",EDGE,"E13.4")])]});
            var Q46;
            Q46=makeQuery(id+"F2.opExtrude","CAP_EDGE",EDGE,{"disambiguationData":[OSD([sQuery(id+"F0.wireOp",EDGE,"E14.1")])],"isStart":false});
            var Q47;
            Q47=makeQuery(id+"F2.opExtrude","SWEPT_EDGE",EDGE,{"disambiguationData":[OSD([sQuery(id+"F0.wireOp",EDGE,"E0.2"),sQuery(id+"F0.wireOp",EDGE,"E15.0"),sQuery(id+"F0.wireOp",EDGE,"E15.1")])]});
            var Q48;
            Q48=makeQuery(id+"F2.opExtrude","SWEPT_EDGE",EDGE,{"disambiguationData":[OSD([sQuery(id+"F0.wireOp",EDGE,"E13.2"),sQuery(id+"F0.wireOp",EDGE,"E13.3")])]});
            var Q49;
            Q49=makeQuery(id+"F1.opExtrude","SWEPT_FACE",FACE,{"disambiguationData":[OSD([sQuery(id+"F0.wireOp",EDGE,"W6VNMVPK-Heu4-H590-lQcW-GhW6zsYcIm86")])]});
            var Q50;
            Q50=makeQuery(id+"F2.opExtrude","CAP_EDGE",EDGE,{"disambiguationData":[OSD([sQuery(id+"F0.wireOp",EDGE,"E15.4")])],"isStart":false});
            var Q51;
            Q51=makeQuery(id+"F2.opExtrude","CAP_EDGE",EDGE,{"disambiguationData":[OSD([sQuery(id+"F0.wireOp",EDGE,"E13.4")])],"isStart":false});
            var Q52;
            Q52=makeQuery(id+"F2.opExtrude","SWEPT_FACE",FACE,{"disambiguationData":[OSD([sQuery(id+"F0.wireOp",EDGE,"E13.4")])]});
            var Q53;
            Q53=makeQuery(id+"F2.opExtrude","SWEPT_EDGE",EDGE,{"disambiguationData":[OSD([sQuery(id+"F0.wireOp",EDGE,"E0.2"),sQuery(id+"F0.wireOp",EDGE,"E15.0"),sQuery(id+"F0.wireOp",EDGE,"E15.5")])]});
            var Q54;
            Q54=makeQuery(id+"F2.opExtrude","CAP_EDGE",EDGE,{"disambiguationData":[OSD([sQuery(id+"F0.wireOp",EDGE,"E13.1")])],"isStart":false});
            var Q55;
            {var subQ0=sQuery(id+"F0.wireOp",EDGE,"E13.0");var subQ1=sQuery(id+"F0.wireOp",EDGE,"E0.0");var subQ2=sQuery(id+"F0.wireOp",EDGE,"E0.5");Q55=makeQuery(id+"F2.boolean.opBoolean","SPLIT",EDGE,{"disambiguationData":[TD([makeQuery(id+"F1.opExtrude","SWEPT_FACE",FACE,{"disambiguationData":[OSD([subQ2])]})])],"derivedFrom":makeQuery(id+"F1.opExtrude","CAP_EDGE",EDGE,{"disambiguationData":[OSD([subQ1,subQ0])],"isStart":false})});}
            var Q56;
            Q56=makeQuery(id+"F2.opExtrude","CAP_EDGE",EDGE,{"disambiguationData":[OSD([sQuery(id+"F0.wireOp",EDGE,"E15.1")])],"isStart":false});
            var Q57;
            Q57=makeQuery(id+"F2.opExtrude","CAP_EDGE",EDGE,{"disambiguationData":[OSD([sQuery(id+"F0.wireOp",EDGE,"E15.3")])],"isStart":false});
            var Q58;
            Q58=makeQuery(id+"F2.boolean.opBoolean","INTERSECT",EDGE,{"derivedFrom":[makeQuery(id+"F1.opExtrude","CAP_FACE",FACE,{"disambiguationData":[OSD([sQuery(id+"F0.wireOp",EDGE,"E0.0"),sQuery(id+"F0.wireOp",EDGE,"E0.1"),sQuery(id+"F0.wireOp",EDGE,"E0.2"),sQuery(id+"F0.wireOp",EDGE,"E0.3"),sQuery(id+"F0.wireOp",EDGE,"E0.4"),sQuery(id+"F0.wireOp",EDGE,"E0.5"),sQuery(id+"F0.wireOp",EDGE,"E1"),sQuery(id+"F0.wireOp",EDGE,"E2"),sQuery(id+"F0.wireOp",EDGE,"E4"),sQuery(id+"F0.wireOp",EDGE,"E5"),sQuery(id+"F0.wireOp",EDGE,"E6"),sQuery(id+"F0.wireOp",EDGE,"E13.0"),sQuery(id+"F0.wireOp",EDGE,"E0.4"),sQuery(id+"F0.wireOp",EDGE,"E15.0"),sQuery(id+"F0.wireOp",EDGE,"W6VNMVPK-Heu4-H590-lQcW-GhW6zsYcIm86"),sQuery(id+"F0.wireOp",EDGE,"E17"),sQuery(id+"F0.wireOp",EDGE,"kWYB9zZw-dUfE-JBuI-mU9n-pgfyDcaRUxvO"),sQuery(id+"F0.wireOp",EDGE,"E18"),sQuery(id+"F0.wireOp",EDGE,"vfnI13aN-5aGC-TwJ9-h9OO-FMGUWFeDmuv9"),sQuery(id+"F0.wireOp",EDGE,"E19"),sQuery(id+"F0.wireOp",EDGE,"E20"),sQuery(id+"F0.wireOp",EDGE,"E21"),sQuery(id+"F0.wireOp",EDGE,"E22"),sQuery(id+"F0.wireOp",EDGE,"JsAoEpAL-XQW4-Lyrg-R8HR-OfjOjkPQAlpN"),sQuery(id+"F0.wireOp",EDGE,"QAwi9ICx-SNt3-gAxD-qMH3-k1r5QHOYkTIN"),sQuery(id+"F0.wireOp",EDGE,"bgABXGzA-3ZDr-4HFO-1yYm-MuwqDgoMTBvo"),sQuery(id+"F0.wireOp",EDGE,"wgyuN0RA-UE8u-KT4Y-o13n-P3vcXdWd7IlJ"),sQuery(id+"F0.wireOp",EDGE,"9d0d2092-a8f3-4ebb-af6d-0df3fb4feacb.trimOffspring"),sQuery(id+"F0.wireOp",EDGE,"10fe8deb-c225-4385-8b94-fba867b40c2d.trimOffspring"),sQuery(id+"F0.wireOp",EDGE,"75751931-a2df-4963-a2bf-7204bff7b78a.filletArc"),sQuery(id+"F0.wireOp",EDGE,"e7d6d30a-f864-4f75-85fc-35ceeb29439c.filletArc"),sQuery(id+"F0.wireOp",EDGE,"a49e830f-b283-406d-92e2-e5d81fe63434.filletArc"),sQuery(id+"F0.wireOp",EDGE,"b3d7f47c-b04d-42dd-9b78-bc98ec63f042.filletArc"),sQuery(id+"F0.wireOp",EDGE,"b51091e8-612c-49d7-9d92-63615423fc4d.filletArc"),sQuery(id+"F0.wireOp",EDGE,"E24.filletArc")])],"isStart":false}),makeQuery(id+"F2.opExtrude","SWEPT_FACE",FACE,{"disambiguationData":[OSD([sQuery(id+"F0.wireOp",EDGE,"E14.4")])]})]});
            var Q59;
            Q59=makeQuery(id+"F2.opExtrude","CAP_EDGE",EDGE,{"disambiguationData":[OSD([sQuery(id+"F0.wireOp",EDGE,"E13.0")])],"isStart":false});
            var Q60;
            Q60=makeQuery(id+"F2.opExtrude","SWEPT_FACE",FACE,{"disambiguationData":[OSD([sQuery(id+"F0.wireOp",EDGE,"E14.4")])]});
            var Q61;
            {var subQ0=sQuery(id+"F0.wireOp",EDGE,"E4");Q61=makeQuery(id+"F2.boolean.opBoolean","MERGE",FACE,{"derivedFrom":[makeQuery(id+"F1.opExtrude","SWEPT_FACE",FACE,{"disambiguationData":[OSD([subQ0])]}),makeQuery(id+"F2.opExtrude","SWEPT_FACE",FACE,{"disambiguationData":[OSD([subQ0])]})]});}
            var Q62;
            Q62=makeQuery(id+"F1.opExtrude","CAP_EDGE",EDGE,{"disambiguationData":[OSD([sQuery(id+"F0.wireOp",EDGE,"E0.3")])],"isStart":false});
            var Q63;
            Q63=makeQuery(id+"F1.opExtrude","SWEPT_FACE",FACE,{"disambiguationData":[OSD([sQuery(id+"F0.wireOp",EDGE,"E17")])]});
            var Q64;
            Q64=makeQuery(id+"F2.opExtrude","CAP_EDGE",EDGE,{"disambiguationData":[OSD([sQuery(id+"F0.wireOp",EDGE,"E4")])],"isStart":false});
            var Q65;
            Q65=makeQuery(id+"F2.opExtrude","SWEPT_EDGE",EDGE,{"disambiguationData":[OSD([sQuery(id+"F0.wireOp",EDGE,"E15.4"),sQuery(id+"F0.wireOp",EDGE,"E15.5")])]});
            var Q66;
            Q66=makeQuery(id+"F2.boolean.opBoolean","INTERSECT",EDGE,{"derivedFrom":[makeQuery(id+"F1.opExtrude","CAP_FACE",FACE,{"disambiguationData":[OSD([sQuery(id+"F0.wireOp",EDGE,"E0.0"),sQuery(id+"F0.wireOp",EDGE,"E0.1"),sQuery(id+"F0.wireOp",EDGE,"E0.2"),sQuery(id+"F0.wireOp",EDGE,"E0.3"),sQuery(id+"F0.wireOp",EDGE,"E0.4"),sQuery(id+"F0.wireOp",EDGE,"E0.5"),sQuery(id+"F0.wireOp",EDGE,"E1"),sQuery(id+"F0.wireOp",EDGE,"E2"),sQuery(id+"F0.wireOp",EDGE,"E4"),sQuery(id+"F0.wireOp",EDGE,"E5"),sQuery(id+"F0.wireOp",EDGE,"E6"),sQuery(id+"F0.wireOp",EDGE,"E13.0"),sQuery(id+"F0.wireOp",EDGE,"E0.4"),sQuery(id+"F0.wireOp",EDGE,"E15.0"),sQuery(id+"F0.wireOp",EDGE,"W6VNMVPK-Heu4-H590-lQcW-GhW6zsYcIm86"),sQuery(id+"F0.wireOp",EDGE,"E17"),sQuery(id+"F0.wireOp",EDGE,"kWYB9zZw-dUfE-JBuI-mU9n-pgfyDcaRUxvO"),sQuery(id+"F0.wireOp",EDGE,"E18"),sQuery(id+"F0.wireOp",EDGE,"vfnI13aN-5aGC-TwJ9-h9OO-FMGUWFeDmuv9"),sQuery(id+"F0.wireOp",EDGE,"E19"),sQuery(id+"F0.wireOp",EDGE,"E20"),sQuery(id+"F0.wireOp",EDGE,"E21"),sQuery(id+"F0.wireOp",EDGE,"E22"),sQuery(id+"F0.wireOp",EDGE,"JsAoEpAL-XQW4-Lyrg-R8HR-OfjOjkPQAlpN"),sQuery(id+"F0.wireOp",EDGE,"QAwi9ICx-SNt3-gAxD-qMH3-k1r5QHOYkTIN"),sQuery(id+"F0.wireOp",EDGE,"bgABXGzA-3ZDr-4HFO-1yYm-MuwqDgoMTBvo"),sQuery(id+"F0.wireOp",EDGE,"wgyuN0RA-UE8u-KT4Y-o13n-P3vcXdWd7IlJ"),sQuery(id+"F0.wireOp",EDGE,"9d0d2092-a8f3-4ebb-af6d-0df3fb4feacb.trimOffspring"),sQuery(id+"F0.wireOp",EDGE,"10fe8deb-c225-4385-8b94-fba867b40c2d.trimOffspring"),sQuery(id+"F0.wireOp",EDGE,"75751931-a2df-4963-a2bf-7204bff7b78a.filletArc"),sQuery(id+"F0.wireOp",EDGE,"e7d6d30a-f864-4f75-85fc-35ceeb29439c.filletArc"),sQuery(id+"F0.wireOp",EDGE,"a49e830f-b283-406d-92e2-e5d81fe63434.filletArc"),sQuery(id+"F0.wireOp",EDGE,"b3d7f47c-b04d-42dd-9b78-bc98ec63f042.filletArc"),sQuery(id+"F0.wireOp",EDGE,"b51091e8-612c-49d7-9d92-63615423fc4d.filletArc"),sQuery(id+"F0.wireOp",EDGE,"E24.filletArc")])],"isStart":false}),makeQuery(id+"F2.opExtrude","SWEPT_FACE",FACE,{"disambiguationData":[OSD([sQuery(id+"F0.wireOp",EDGE,"E13.3")])]})]});
            var Q67;
            Q67=makeQuery(id+"F2.opExtrude","SWEPT_EDGE",EDGE,{"disambiguationData":[OSD([sQuery(id+"F0.wireOp",EDGE,"E0.0"),sQuery(id+"F0.wireOp",EDGE,"E13.0"),sQuery(id+"F0.wireOp",EDGE,"E13.1")])]});
            var Q68;
            Q68=makeQuery(id+"F1.opExtrude","CAP_EDGE",EDGE,{"disambiguationData":[OSD([sQuery(id+"F0.wireOp",EDGE,"E0.4"),sQuery(id+"F0.wireOp",EDGE,"E0.4")])],"isStart":true});
            var Q69;
            Q69=makeQuery(id+"F2.opExtrude","CAP_EDGE",EDGE,{"disambiguationData":[OSD([sQuery(id+"F0.wireOp",EDGE,"E14.4")])],"isStart":false});
            var Q70;
            Q70=makeQuery(id+"F2.boolean.opBoolean","INTERSECT",EDGE,{"derivedFrom":[makeQuery(id+"F1.opExtrude","CAP_FACE",FACE,{"disambiguationData":[OSD([sQuery(id+"F0.wireOp",EDGE,"E0.0"),sQuery(id+"F0.wireOp",EDGE,"E0.1"),sQuery(id+"F0.wireOp",EDGE,"E0.2"),sQuery(id+"F0.wireOp",EDGE,"E0.3"),sQuery(id+"F0.wireOp",EDGE,"E0.4"),sQuery(id+"F0.wireOp",EDGE,"E0.5"),sQuery(id+"F0.wireOp",EDGE,"E1"),sQuery(id+"F0.wireOp",EDGE,"E2"),sQuery(id+"F0.wireOp",EDGE,"E4"),sQuery(id+"F0.wireOp",EDGE,"E5"),sQuery(id+"F0.wireOp",EDGE,"E6"),sQuery(id+"F0.wireOp",EDGE,"E13.0"),sQuery(id+"F0.wireOp",EDGE,"E0.4"),sQuery(id+"F0.wireOp",EDGE,"E15.0"),sQuery(id+"F0.wireOp",EDGE,"W6VNMVPK-Heu4-H590-lQcW-GhW6zsYcIm86"),sQuery(id+"F0.wireOp",EDGE,"E17"),sQuery(id+"F0.wireOp",EDGE,"kWYB9zZw-dUfE-JBuI-mU9n-pgfyDcaRUxvO"),sQuery(id+"F0.wireOp",EDGE,"E18"),sQuery(id+"F0.wireOp",EDGE,"vfnI13aN-5aGC-TwJ9-h9OO-FMGUWFeDmuv9"),sQuery(id+"F0.wireOp",EDGE,"E19"),sQuery(id+"F0.wireOp",EDGE,"E20"),sQuery(id+"F0.wireOp",EDGE,"E21"),sQuery(id+"F0.wireOp",EDGE,"E22"),sQuery(id+"F0.wireOp",EDGE,"JsAoEpAL-XQW4-Lyrg-R8HR-OfjOjkPQAlpN"),sQuery(id+"F0.wireOp",EDGE,"QAwi9ICx-SNt3-gAxD-qMH3-k1r5QHOYkTIN"),sQuery(id+"F0.wireOp",EDGE,"bgABXGzA-3ZDr-4HFO-1yYm-MuwqDgoMTBvo"),sQuery(id+"F0.wireOp",EDGE,"wgyuN0RA-UE8u-KT4Y-o13n-P3vcXdWd7IlJ"),sQuery(id+"F0.wireOp",EDGE,"9d0d2092-a8f3-4ebb-af6d-0df3fb4feacb.trimOffspring"),sQuery(id+"F0.wireOp",EDGE,"10fe8deb-c225-4385-8b94-fba867b40c2d.trimOffspring"),sQuery(id+"F0.wireOp",EDGE,"75751931-a2df-4963-a2bf-7204bff7b78a.filletArc"),sQuery(id+"F0.wireOp",EDGE,"e7d6d30a-f864-4f75-85fc-35ceeb29439c.filletArc"),sQuery(id+"F0.wireOp",EDGE,"a49e830f-b283-406d-92e2-e5d81fe63434.filletArc"),sQuery(id+"F0.wireOp",EDGE,"b3d7f47c-b04d-42dd-9b78-bc98ec63f042.filletArc"),sQuery(id+"F0.wireOp",EDGE,"b51091e8-612c-49d7-9d92-63615423fc4d.filletArc"),sQuery(id+"F0.wireOp",EDGE,"E24.filletArc")])],"isStart":false}),makeQuery(id+"F2.opExtrude","SWEPT_FACE",FACE,{"disambiguationData":[OSD([sQuery(id+"F0.wireOp",EDGE,"E15.4")])]})]});
            var Q71;
            Q71=makeQuery(id+"F1.opExtrude","CAP_EDGE",EDGE,{"disambiguationData":[OSD([sQuery(id+"F0.wireOp",EDGE,"E0.0"),sQuery(id+"F0.wireOp",EDGE,"E13.0")])],"isStart":true});
            var Q72;
            {var subQ0=sQuery(id+"F0.wireOp",EDGE,"E6");Q72=makeQuery(id+"F2.boolean.opBoolean","MERGE",FACE,{"derivedFrom":[makeQuery(id+"F1.opExtrude","SWEPT_FACE",FACE,{"disambiguationData":[OSD([subQ0])]}),makeQuery(id+"F2.opExtrude","SWEPT_FACE",FACE,{"disambiguationData":[OSD([subQ0])]})]});}
            var Q73;
            Q73=makeQuery(id+"F2.boolean.opBoolean","INTERSECT",EDGE,{"derivedFrom":[makeQuery(id+"F1.opExtrude","CAP_FACE",FACE,{"disambiguationData":[OSD([sQuery(id+"F0.wireOp",EDGE,"E0.0"),sQuery(id+"F0.wireOp",EDGE,"E0.1"),sQuery(id+"F0.wireOp",EDGE,"E0.2"),sQuery(id+"F0.wireOp",EDGE,"E0.3"),sQuery(id+"F0.wireOp",EDGE,"E0.4"),sQuery(id+"F0.wireOp",EDGE,"E0.5"),sQuery(id+"F0.wireOp",EDGE,"E1"),sQuery(id+"F0.wireOp",EDGE,"E2"),sQuery(id+"F0.wireOp",EDGE,"E4"),sQuery(id+"F0.wireOp",EDGE,"E5"),sQuery(id+"F0.wireOp",EDGE,"E6"),sQuery(id+"F0.wireOp",EDGE,"E13.0"),sQuery(id+"F0.wireOp",EDGE,"E0.4"),sQuery(id+"F0.wireOp",EDGE,"E15.0"),sQuery(id+"F0.wireOp",EDGE,"W6VNMVPK-Heu4-H590-lQcW-GhW6zsYcIm86"),sQuery(id+"F0.wireOp",EDGE,"E17"),sQuery(id+"F0.wireOp",EDGE,"kWYB9zZw-dUfE-JBuI-mU9n-pgfyDcaRUxvO"),sQuery(id+"F0.wireOp",EDGE,"E18"),sQuery(id+"F0.wireOp",EDGE,"vfnI13aN-5aGC-TwJ9-h9OO-FMGUWFeDmuv9"),sQuery(id+"F0.wireOp",EDGE,"E19"),sQuery(id+"F0.wireOp",EDGE,"E20"),sQuery(id+"F0.wireOp",EDGE,"E21"),sQuery(id+"F0.wireOp",EDGE,"E22"),sQuery(id+"F0.wireOp",EDGE,"JsAoEpAL-XQW4-Lyrg-R8HR-OfjOjkPQAlpN"),sQuery(id+"F0.wireOp",EDGE,"QAwi9ICx-SNt3-gAxD-qMH3-k1r5QHOYkTIN"),sQuery(id+"F0.wireOp",EDGE,"bgABXGzA-3ZDr-4HFO-1yYm-MuwqDgoMTBvo"),sQuery(id+"F0.wireOp",EDGE,"wgyuN0RA-UE8u-KT4Y-o13n-P3vcXdWd7IlJ"),sQuery(id+"F0.wireOp",EDGE,"9d0d2092-a8f3-4ebb-af6d-0df3fb4feacb.trimOffspring"),sQuery(id+"F0.wireOp",EDGE,"10fe8deb-c225-4385-8b94-fba867b40c2d.trimOffspring"),sQuery(id+"F0.wireOp",EDGE,"75751931-a2df-4963-a2bf-7204bff7b78a.filletArc"),sQuery(id+"F0.wireOp",EDGE,"e7d6d30a-f864-4f75-85fc-35ceeb29439c.filletArc"),sQuery(id+"F0.wireOp",EDGE,"a49e830f-b283-406d-92e2-e5d81fe63434.filletArc"),sQuery(id+"F0.wireOp",EDGE,"b3d7f47c-b04d-42dd-9b78-bc98ec63f042.filletArc"),sQuery(id+"F0.wireOp",EDGE,"b51091e8-612c-49d7-9d92-63615423fc4d.filletArc"),sQuery(id+"F0.wireOp",EDGE,"E24.filletArc")])],"isStart":false}),makeQuery(id+"F2.opExtrude","SWEPT_FACE",FACE,{"disambiguationData":[OSD([sQuery(id+"F0.wireOp",EDGE,"E15.5")])]})]});
            var Q74;
            Q74=makeQuery(id+"F2.boolean.opBoolean","INTERSECT",EDGE,{"derivedFrom":[makeQuery(id+"F1.opExtrude","CAP_FACE",FACE,{"disambiguationData":[OSD([sQuery(id+"F0.wireOp",EDGE,"E0.0"),sQuery(id+"F0.wireOp",EDGE,"E0.1"),sQuery(id+"F0.wireOp",EDGE,"E0.2"),sQuery(id+"F0.wireOp",EDGE,"E0.3"),sQuery(id+"F0.wireOp",EDGE,"E0.4"),sQuery(id+"F0.wireOp",EDGE,"E0.5"),sQuery(id+"F0.wireOp",EDGE,"E1"),sQuery(id+"F0.wireOp",EDGE,"E2"),sQuery(id+"F0.wireOp",EDGE,"E4"),sQuery(id+"F0.wireOp",EDGE,"E5"),sQuery(id+"F0.wireOp",EDGE,"E6"),sQuery(id+"F0.wireOp",EDGE,"E13.0"),sQuery(id+"F0.wireOp",EDGE,"E0.4"),sQuery(id+"F0.wireOp",EDGE,"E15.0"),sQuery(id+"F0.wireOp",EDGE,"W6VNMVPK-Heu4-H590-lQcW-GhW6zsYcIm86"),sQuery(id+"F0.wireOp",EDGE,"E17"),sQuery(id+"F0.wireOp",EDGE,"kWYB9zZw-dUfE-JBuI-mU9n-pgfyDcaRUxvO"),sQuery(id+"F0.wireOp",EDGE,"E18"),sQuery(id+"F0.wireOp",EDGE,"vfnI13aN-5aGC-TwJ9-h9OO-FMGUWFeDmuv9"),sQuery(id+"F0.wireOp",EDGE,"E19"),sQuery(id+"F0.wireOp",EDGE,"E20"),sQuery(id+"F0.wireOp",EDGE,"E21"),sQuery(id+"F0.wireOp",EDGE,"E22"),sQuery(id+"F0.wireOp",EDGE,"JsAoEpAL-XQW4-Lyrg-R8HR-OfjOjkPQAlpN"),sQuery(id+"F0.wireOp",EDGE,"QAwi9ICx-SNt3-gAxD-qMH3-k1r5QHOYkTIN"),sQuery(id+"F0.wireOp",EDGE,"bgABXGzA-3ZDr-4HFO-1yYm-MuwqDgoMTBvo"),sQuery(id+"F0.wireOp",EDGE,"wgyuN0RA-UE8u-KT4Y-o13n-P3vcXdWd7IlJ"),sQuery(id+"F0.wireOp",EDGE,"9d0d2092-a8f3-4ebb-af6d-0df3fb4feacb.trimOffspring"),sQuery(id+"F0.wireOp",EDGE,"10fe8deb-c225-4385-8b94-fba867b40c2d.trimOffspring"),sQuery(id+"F0.wireOp",EDGE,"75751931-a2df-4963-a2bf-7204bff7b78a.filletArc"),sQuery(id+"F0.wireOp",EDGE,"e7d6d30a-f864-4f75-85fc-35ceeb29439c.filletArc"),sQuery(id+"F0.wireOp",EDGE,"a49e830f-b283-406d-92e2-e5d81fe63434.filletArc"),sQuery(id+"F0.wireOp",EDGE,"b3d7f47c-b04d-42dd-9b78-bc98ec63f042.filletArc"),sQuery(id+"F0.wireOp",EDGE,"b51091e8-612c-49d7-9d92-63615423fc4d.filletArc"),sQuery(id+"F0.wireOp",EDGE,"E24.filletArc")])],"isStart":false}),makeQuery(id+"F2.opExtrude","SWEPT_FACE",FACE,{"disambiguationData":[OSD([sQuery(id+"F0.wireOp",EDGE,"E14.2")])]})]});
            var Q75;
            Q75=makeQuery(id+"F1.opExtrude","SWEPT_EDGE",EDGE,{"disambiguationData":[OSD([sQuery(id+"F0.wireOp",EDGE,"E0.2"),sQuery(id+"F0.wireOp",EDGE,"E0.3")])]});
            var Q76;
            Q76=makeQuery(id+"F2.opExtrude","SWEPT_FACE",FACE,{"disambiguationData":[OSD([sQuery(id+"F0.wireOp",EDGE,"E14.2")])]});
            var Q77;
            Q77=makeQuery(id+"F2.opExtrude","SWEPT_EDGE",EDGE,{"disambiguationData":[OSD([sQuery(id+"F0.wireOp",EDGE,"E14.1"),sQuery(id+"F0.wireOp",EDGE,"E14.2")])]});
            var Q78;
            Q78=makeQuery(id+"F2.opExtrude","SWEPT_EDGE",EDGE,{"disambiguationData":[OSD([sQuery(id+"F0.wireOp",EDGE,"E0.0"),sQuery(id+"F0.wireOp",EDGE,"E13.0"),sQuery(id+"F0.wireOp",EDGE,"E13.5")])]});
            var Q79;
            Q79=makeQuery(id+"F1.opExtrude","SWEPT_EDGE",EDGE,{"disambiguationData":[OSD([sQuery(id+"F0.wireOp",EDGE,"E0.0"),sQuery(id+"F0.wireOp",EDGE,"E0.1")])]});
            var Q80;
            Q80=makeQuery(id+"F1.opExtrude","CAP_EDGE",EDGE,{"disambiguationData":[OSD([sQuery(id+"F0.wireOp",EDGE,"E17")])],"isStart":true});
            var Q81;
            Q81=makeQuery(id+"F1.opExtrude","CAP_EDGE",EDGE,{"disambiguationData":[OSD([sQuery(id+"F0.wireOp",EDGE,"kWYB9zZw-dUfE-JBuI-mU9n-pgfyDcaRUxvO")])],"isStart":true});
            var Q82;
            Q82=makeQuery(id+"F2.opExtrude","SWEPT_EDGE",EDGE,{"disambiguationData":[OSD([sQuery(id+"F0.wireOp",EDGE,"E14.2"),sQuery(id+"F0.wireOp",EDGE,"E14.3")])]});
            var Q83;
            Q83=makeQuery(id+"F1.opExtrude","CAP_EDGE",EDGE,{"disambiguationData":[OSD([sQuery(id+"F0.wireOp",EDGE,"E0.1")])],"isStart":true});
            var Q84;
            Q84=makeQuery(id+"F2.boolean.opBoolean","INTERSECT",EDGE,{"derivedFrom":[makeQuery(id+"F1.opExtrude","CAP_FACE",FACE,{"disambiguationData":[OSD([sQuery(id+"F0.wireOp",EDGE,"E0.0"),sQuery(id+"F0.wireOp",EDGE,"E0.1"),sQuery(id+"F0.wireOp",EDGE,"E0.2"),sQuery(id+"F0.wireOp",EDGE,"E0.3"),sQuery(id+"F0.wireOp",EDGE,"E0.4"),sQuery(id+"F0.wireOp",EDGE,"E0.5"),sQuery(id+"F0.wireOp",EDGE,"E1"),sQuery(id+"F0.wireOp",EDGE,"E2"),sQuery(id+"F0.wireOp",EDGE,"E4"),sQuery(id+"F0.wireOp",EDGE,"E5"),sQuery(id+"F0.wireOp",EDGE,"E6"),sQuery(id+"F0.wireOp",EDGE,"E13.0"),sQuery(id+"F0.wireOp",EDGE,"E0.4"),sQuery(id+"F0.wireOp",EDGE,"E15.0"),sQuery(id+"F0.wireOp",EDGE,"W6VNMVPK-Heu4-H590-lQcW-GhW6zsYcIm86"),sQuery(id+"F0.wireOp",EDGE,"E17"),sQuery(id+"F0.wireOp",EDGE,"kWYB9zZw-dUfE-JBuI-mU9n-pgfyDcaRUxvO"),sQuery(id+"F0.wireOp",EDGE,"E18"),sQuery(id+"F0.wireOp",EDGE,"vfnI13aN-5aGC-TwJ9-h9OO-FMGUWFeDmuv9"),sQuery(id+"F0.wireOp",EDGE,"E19"),sQuery(id+"F0.wireOp",EDGE,"E20"),sQuery(id+"F0.wireOp",EDGE,"E21"),sQuery(id+"F0.wireOp",EDGE,"E22"),sQuery(id+"F0.wireOp",EDGE,"JsAoEpAL-XQW4-Lyrg-R8HR-OfjOjkPQAlpN"),sQuery(id+"F0.wireOp",EDGE,"QAwi9ICx-SNt3-gAxD-qMH3-k1r5QHOYkTIN"),sQuery(id+"F0.wireOp",EDGE,"bgABXGzA-3ZDr-4HFO-1yYm-MuwqDgoMTBvo"),sQuery(id+"F0.wireOp",EDGE,"wgyuN0RA-UE8u-KT4Y-o13n-P3vcXdWd7IlJ"),sQuery(id+"F0.wireOp",EDGE,"9d0d2092-a8f3-4ebb-af6d-0df3fb4feacb.trimOffspring"),sQuery(id+"F0.wireOp",EDGE,"10fe8deb-c225-4385-8b94-fba867b40c2d.trimOffspring"),sQuery(id+"F0.wireOp",EDGE,"75751931-a2df-4963-a2bf-7204bff7b78a.filletArc"),sQuery(id+"F0.wireOp",EDGE,"e7d6d30a-f864-4f75-85fc-35ceeb29439c.filletArc"),sQuery(id+"F0.wireOp",EDGE,"a49e830f-b283-406d-92e2-e5d81fe63434.filletArc"),sQuery(id+"F0.wireOp",EDGE,"b3d7f47c-b04d-42dd-9b78-bc98ec63f042.filletArc"),sQuery(id+"F0.wireOp",EDGE,"b51091e8-612c-49d7-9d92-63615423fc4d.filletArc"),sQuery(id+"F0.wireOp",EDGE,"E24.filletArc")])],"isStart":false}),makeQuery(id+"F2.opExtrude","SWEPT_FACE",FACE,{"disambiguationData":[OSD([sQuery(id+"F0.wireOp",EDGE,"E13.4")])]})]});
            var Q85;
            Q85=makeQuery(id+"F1.opExtrude","CAP_EDGE",EDGE,{"disambiguationData":[OSD([sQuery(id+"F0.wireOp",EDGE,"E0.2"),sQuery(id+"F0.wireOp",EDGE,"E15.0")])],"isStart":true});
            var Q86;
            Q86=makeQuery(id+"F1.opExtrude","SWEPT_EDGE",EDGE,{"disambiguationData":[OSD([sQuery(id+"F0.wireOp",EDGE,"E0.0"),sQuery(id+"F0.wireOp",EDGE,"E0.5")])]});
            var Q87;
            Q87=makeQuery(id+"F2.boolean.opBoolean","INTERSECT",EDGE,{"derivedFrom":[makeQuery(id+"F1.opExtrude","CAP_FACE",FACE,{"disambiguationData":[OSD([sQuery(id+"F0.wireOp",EDGE,"E0.0"),sQuery(id+"F0.wireOp",EDGE,"E0.1"),sQuery(id+"F0.wireOp",EDGE,"E0.2"),sQuery(id+"F0.wireOp",EDGE,"E0.3"),sQuery(id+"F0.wireOp",EDGE,"E0.4"),sQuery(id+"F0.wireOp",EDGE,"E0.5"),sQuery(id+"F0.wireOp",EDGE,"E1"),sQuery(id+"F0.wireOp",EDGE,"E2"),sQuery(id+"F0.wireOp",EDGE,"E4"),sQuery(id+"F0.wireOp",EDGE,"E5"),sQuery(id+"F0.wireOp",EDGE,"E6"),sQuery(id+"F0.wireOp",EDGE,"E13.0"),sQuery(id+"F0.wireOp",EDGE,"E0.4"),sQuery(id+"F0.wireOp",EDGE,"E15.0"),sQuery(id+"F0.wireOp",EDGE,"W6VNMVPK-Heu4-H590-lQcW-GhW6zsYcIm86"),sQuery(id+"F0.wireOp",EDGE,"E17"),sQuery(id+"F0.wireOp",EDGE,"kWYB9zZw-dUfE-JBuI-mU9n-pgfyDcaRUxvO"),sQuery(id+"F0.wireOp",EDGE,"E18"),sQuery(id+"F0.wireOp",EDGE,"vfnI13aN-5aGC-TwJ9-h9OO-FMGUWFeDmuv9"),sQuery(id+"F0.wireOp",EDGE,"E19"),sQuery(id+"F0.wireOp",EDGE,"E20"),sQuery(id+"F0.wireOp",EDGE,"E21"),sQuery(id+"F0.wireOp",EDGE,"E22"),sQuery(id+"F0.wireOp",EDGE,"JsAoEpAL-XQW4-Lyrg-R8HR-OfjOjkPQAlpN"),sQuery(id+"F0.wireOp",EDGE,"QAwi9ICx-SNt3-gAxD-qMH3-k1r5QHOYkTIN"),sQuery(id+"F0.wireOp",EDGE,"bgABXGzA-3ZDr-4HFO-1yYm-MuwqDgoMTBvo"),sQuery(id+"F0.wireOp",EDGE,"wgyuN0RA-UE8u-KT4Y-o13n-P3vcXdWd7IlJ"),sQuery(id+"F0.wireOp",EDGE,"9d0d2092-a8f3-4ebb-af6d-0df3fb4feacb.trimOffspring"),sQuery(id+"F0.wireOp",EDGE,"10fe8deb-c225-4385-8b94-fba867b40c2d.trimOffspring"),sQuery(id+"F0.wireOp",EDGE,"75751931-a2df-4963-a2bf-7204bff7b78a.filletArc"),sQuery(id+"F0.wireOp",EDGE,"e7d6d30a-f864-4f75-85fc-35ceeb29439c.filletArc"),sQuery(id+"F0.wireOp",EDGE,"a49e830f-b283-406d-92e2-e5d81fe63434.filletArc"),sQuery(id+"F0.wireOp",EDGE,"b3d7f47c-b04d-42dd-9b78-bc98ec63f042.filletArc"),sQuery(id+"F0.wireOp",EDGE,"b51091e8-612c-49d7-9d92-63615423fc4d.filletArc"),sQuery(id+"F0.wireOp",EDGE,"E24.filletArc")])],"isStart":false}),makeQuery(id+"F2.opExtrude","SWEPT_FACE",FACE,{"disambiguationData":[OSD([sQuery(id+"F0.wireOp",EDGE,"E13.5")])]})]});
            var Q88;
            Q88=makeQuery(id+"F2.boolean.opBoolean","INTERSECT",EDGE,{"derivedFrom":[makeQuery(id+"F1.opExtrude","CAP_FACE",FACE,{"disambiguationData":[OSD([sQuery(id+"F0.wireOp",EDGE,"E0.0"),sQuery(id+"F0.wireOp",EDGE,"E0.1"),sQuery(id+"F0.wireOp",EDGE,"E0.2"),sQuery(id+"F0.wireOp",EDGE,"E0.3"),sQuery(id+"F0.wireOp",EDGE,"E0.4"),sQuery(id+"F0.wireOp",EDGE,"E0.5"),sQuery(id+"F0.wireOp",EDGE,"E1"),sQuery(id+"F0.wireOp",EDGE,"E2"),sQuery(id+"F0.wireOp",EDGE,"E4"),sQuery(id+"F0.wireOp",EDGE,"E5"),sQuery(id+"F0.wireOp",EDGE,"E6"),sQuery(id+"F0.wireOp",EDGE,"E13.0"),sQuery(id+"F0.wireOp",EDGE,"E0.4"),sQuery(id+"F0.wireOp",EDGE,"E15.0"),sQuery(id+"F0.wireOp",EDGE,"W6VNMVPK-Heu4-H590-lQcW-GhW6zsYcIm86"),sQuery(id+"F0.wireOp",EDGE,"E17"),sQuery(id+"F0.wireOp",EDGE,"kWYB9zZw-dUfE-JBuI-mU9n-pgfyDcaRUxvO"),sQuery(id+"F0.wireOp",EDGE,"E18"),sQuery(id+"F0.wireOp",EDGE,"vfnI13aN-5aGC-TwJ9-h9OO-FMGUWFeDmuv9"),sQuery(id+"F0.wireOp",EDGE,"E19"),sQuery(id+"F0.wireOp",EDGE,"E20"),sQuery(id+"F0.wireOp",EDGE,"E21"),sQuery(id+"F0.wireOp",EDGE,"E22"),sQuery(id+"F0.wireOp",EDGE,"JsAoEpAL-XQW4-Lyrg-R8HR-OfjOjkPQAlpN"),sQuery(id+"F0.wireOp",EDGE,"QAwi9ICx-SNt3-gAxD-qMH3-k1r5QHOYkTIN"),sQuery(id+"F0.wireOp",EDGE,"bgABXGzA-3ZDr-4HFO-1yYm-MuwqDgoMTBvo"),sQuery(id+"F0.wireOp",EDGE,"wgyuN0RA-UE8u-KT4Y-o13n-P3vcXdWd7IlJ"),sQuery(id+"F0.wireOp",EDGE,"9d0d2092-a8f3-4ebb-af6d-0df3fb4feacb.trimOffspring"),sQuery(id+"F0.wireOp",EDGE,"10fe8deb-c225-4385-8b94-fba867b40c2d.trimOffspring"),sQuery(id+"F0.wireOp",EDGE,"75751931-a2df-4963-a2bf-7204bff7b78a.filletArc"),sQuery(id+"F0.wireOp",EDGE,"e7d6d30a-f864-4f75-85fc-35ceeb29439c.filletArc"),sQuery(id+"F0.wireOp",EDGE,"a49e830f-b283-406d-92e2-e5d81fe63434.filletArc"),sQuery(id+"F0.wireOp",EDGE,"b3d7f47c-b04d-42dd-9b78-bc98ec63f042.filletArc"),sQuery(id+"F0.wireOp",EDGE,"b51091e8-612c-49d7-9d92-63615423fc4d.filletArc"),sQuery(id+"F0.wireOp",EDGE,"E24.filletArc")])],"isStart":false}),makeQuery(id+"F2.opExtrude","SWEPT_FACE",FACE,{"disambiguationData":[OSD([sQuery(id+"F0.wireOp",EDGE,"E13.1")])]})]});
            var Q89;
            Q89=makeQuery(id+"F2.opExtrude","SWEPT_EDGE",EDGE,{"disambiguationData":[OSD([sQuery(id+"F0.wireOp",EDGE,"E15.1"),sQuery(id+"F0.wireOp",EDGE,"E15.2")])]});
            var Q90;
            {var subQ0=sQuery(id+"F0.wireOp",EDGE,"E15.0");var subQ1=sQuery(id+"F0.wireOp",EDGE,"E0.1");var subQ2=sQuery(id+"F0.wireOp",EDGE,"E0.2");Q90=makeQuery(id+"F2.boolean.opBoolean","SPLIT",EDGE,{"disambiguationData":[TD([makeQuery(id+"F1.opExtrude","SWEPT_FACE",FACE,{"disambiguationData":[OSD([subQ1])]})])],"derivedFrom":makeQuery(id+"F1.opExtrude","CAP_EDGE",EDGE,{"disambiguationData":[OSD([subQ2,subQ0])],"isStart":false})});}
            var Q91;
            Q91=makeQuery(id+"F1.opExtrude","CAP_EDGE",EDGE,{"disambiguationData":[OSD([sQuery(id+"F0.wireOp",EDGE,"E0.5")])],"isStart":false});
            var Q92;
            Q92=makeQuery(id+"F2.opExtrude","SWEPT_FACE",FACE,{"disambiguationData":[OSD([sQuery(id+"F0.wireOp",EDGE,"E15.4")])]});
            var Q93;
            Q93=makeQuery(id+"F1.opExtrude","SWEPT_FACE",FACE,{"disambiguationData":[OSD([sQuery(id+"F0.wireOp",EDGE,"E20")])]});
            var Q94;
            Q94=makeQuery(id+"F1.opExtrude","SWEPT_FACE",FACE,{"disambiguationData":[OSD([sQuery(id+"F0.wireOp",EDGE,"E19")])]});
            var Q95;
            Q95=makeQuery(id+"F1.opExtrude","SWEPT_EDGE",EDGE,{"disambiguationData":[OSD([sQuery(id+"F0.wireOp",EDGE,"E0.4"),sQuery(id+"F0.wireOp",EDGE,"E0.5")])]});
            var Q96;
            Q96=makeQuery(id+"F1.opExtrude","CAP_EDGE",EDGE,{"disambiguationData":[OSD([sQuery(id+"F0.wireOp",EDGE,"W6VNMVPK-Heu4-H590-lQcW-GhW6zsYcIm86")])],"isStart":true});
            var Q97;
            Q97=makeQuery(id+"F2.opExtrude","CAP_EDGE",EDGE,{"disambiguationData":[OSD([sQuery(id+"F0.wireOp",EDGE,"E5")])],"isStart":false});
            var Q98;
            Q98=makeQuery(id+"F2.opExtrude","SWEPT_FACE",FACE,{"disambiguationData":[OSD([sQuery(id+"F0.wireOp",EDGE,"E13.5")])]});
            var Q99;
            Q99=makeQuery(id+"F1.opExtrude","SWEPT_EDGE",EDGE,{"disambiguationData":[OSD([sQuery(id+"F0.wireOp",EDGE,"E0.1"),sQuery(id+"F0.wireOp",EDGE,"E0.2")])]});
            var Q100;
            Q100=makeQuery(id+"F1.opExtrude","SWEPT_FACE",FACE,{"disambiguationData":[OSD([sQuery(id+"F0.wireOp",EDGE,"E18")])]});
            var Q101;
            Q101=makeQuery(id+"F1.opExtrude","SWEPT_FACE",FACE,{"disambiguationData":[OSD([sQuery(id+"F0.wireOp",EDGE,"kWYB9zZw-dUfE-JBuI-mU9n-pgfyDcaRUxvO")])]});
            var Q102;
            Q102=makeQuery(id+"F2.opExtrude","SWEPT_FACE",FACE,{"disambiguationData":[OSD([sQuery(id+"F0.wireOp",EDGE,"E15.3")])]});
            var Q103;
            Q103=makeQuery(id+"F1.opExtrude","SWEPT_EDGE",EDGE,{"disambiguationData":[OSD([sQuery(id+"F0.wireOp",EDGE,"W6VNMVPK-Heu4-H590-lQcW-GhW6zsYcIm86"),sQuery(id+"F0.wireOp",EDGE,"E17")])]});
            var Q104;
            Q104=makeQuery(id+"F2.opExtrude","CAP_EDGE",EDGE,{"disambiguationData":[OSD([sQuery(id+"F0.wireOp",EDGE,"E15.0")])],"isStart":false});
            var Q105;
            Q105=makeQuery(id+"F1.opExtrude","SWEPT_FACE",FACE,{"disambiguationData":[OSD([sQuery(id+"F0.wireOp",EDGE,"E1")])]});
            var Q106;
            Q106=makeQuery(id+"F2.boolean.opBoolean","INTERSECT",EDGE,{"derivedFrom":[makeQuery(id+"F1.opExtrude","CAP_FACE",FACE,{"disambiguationData":[OSD([sQuery(id+"F0.wireOp",EDGE,"E0.0"),sQuery(id+"F0.wireOp",EDGE,"E0.1"),sQuery(id+"F0.wireOp",EDGE,"E0.2"),sQuery(id+"F0.wireOp",EDGE,"E0.3"),sQuery(id+"F0.wireOp",EDGE,"E0.4"),sQuery(id+"F0.wireOp",EDGE,"E0.5"),sQuery(id+"F0.wireOp",EDGE,"E1"),sQuery(id+"F0.wireOp",EDGE,"E2"),sQuery(id+"F0.wireOp",EDGE,"E4"),sQuery(id+"F0.wireOp",EDGE,"E5"),sQuery(id+"F0.wireOp",EDGE,"E6"),sQuery(id+"F0.wireOp",EDGE,"E13.0"),sQuery(id+"F0.wireOp",EDGE,"E0.4"),sQuery(id+"F0.wireOp",EDGE,"E15.0"),sQuery(id+"F0.wireOp",EDGE,"W6VNMVPK-Heu4-H590-lQcW-GhW6zsYcIm86"),sQuery(id+"F0.wireOp",EDGE,"E17"),sQuery(id+"F0.wireOp",EDGE,"kWYB9zZw-dUfE-JBuI-mU9n-pgfyDcaRUxvO"),sQuery(id+"F0.wireOp",EDGE,"E18"),sQuery(id+"F0.wireOp",EDGE,"vfnI13aN-5aGC-TwJ9-h9OO-FMGUWFeDmuv9"),sQuery(id+"F0.wireOp",EDGE,"E19"),sQuery(id+"F0.wireOp",EDGE,"E20"),sQuery(id+"F0.wireOp",EDGE,"E21"),sQuery(id+"F0.wireOp",EDGE,"E22"),sQuery(id+"F0.wireOp",EDGE,"JsAoEpAL-XQW4-Lyrg-R8HR-OfjOjkPQAlpN"),sQuery(id+"F0.wireOp",EDGE,"QAwi9ICx-SNt3-gAxD-qMH3-k1r5QHOYkTIN"),sQuery(id+"F0.wireOp",EDGE,"bgABXGzA-3ZDr-4HFO-1yYm-MuwqDgoMTBvo"),sQuery(id+"F0.wireOp",EDGE,"wgyuN0RA-UE8u-KT4Y-o13n-P3vcXdWd7IlJ"),sQuery(id+"F0.wireOp",EDGE,"9d0d2092-a8f3-4ebb-af6d-0df3fb4feacb.trimOffspring"),sQuery(id+"F0.wireOp",EDGE,"10fe8deb-c225-4385-8b94-fba867b40c2d.trimOffspring"),sQuery(id+"F0.wireOp",EDGE,"75751931-a2df-4963-a2bf-7204bff7b78a.filletArc"),sQuery(id+"F0.wireOp",EDGE,"e7d6d30a-f864-4f75-85fc-35ceeb29439c.filletArc"),sQuery(id+"F0.wireOp",EDGE,"a49e830f-b283-406d-92e2-e5d81fe63434.filletArc"),sQuery(id+"F0.wireOp",EDGE,"b3d7f47c-b04d-42dd-9b78-bc98ec63f042.filletArc"),sQuery(id+"F0.wireOp",EDGE,"b51091e8-612c-49d7-9d92-63615423fc4d.filletArc"),sQuery(id+"F0.wireOp",EDGE,"E24.filletArc")])],"isStart":false}),makeQuery(id+"F2.opExtrude","SWEPT_FACE",FACE,{"disambiguationData":[OSD([sQuery(id+"F0.wireOp",EDGE,"E15.3")])]})]});
            var Q107;
            Q107=makeQuery(id+"F1.opExtrude","CAP_EDGE",EDGE,{"disambiguationData":[OSD([sQuery(id+"F0.wireOp",EDGE,"E0.3")])],"isStart":true});
            var Q108;
            Q108=makeQuery(id+"F2.boolean.opBoolean","INTERSECT",EDGE,{"derivedFrom":[makeQuery(id+"F1.opExtrude","CAP_FACE",FACE,{"disambiguationData":[OSD([sQuery(id+"F0.wireOp",EDGE,"E0.0"),sQuery(id+"F0.wireOp",EDGE,"E0.1"),sQuery(id+"F0.wireOp",EDGE,"E0.2"),sQuery(id+"F0.wireOp",EDGE,"E0.3"),sQuery(id+"F0.wireOp",EDGE,"E0.4"),sQuery(id+"F0.wireOp",EDGE,"E0.5"),sQuery(id+"F0.wireOp",EDGE,"E1"),sQuery(id+"F0.wireOp",EDGE,"E2"),sQuery(id+"F0.wireOp",EDGE,"E4"),sQuery(id+"F0.wireOp",EDGE,"E5"),sQuery(id+"F0.wireOp",EDGE,"E6"),sQuery(id+"F0.wireOp",EDGE,"E13.0"),sQuery(id+"F0.wireOp",EDGE,"E0.4"),sQuery(id+"F0.wireOp",EDGE,"E15.0"),sQuery(id+"F0.wireOp",EDGE,"W6VNMVPK-Heu4-H590-lQcW-GhW6zsYcIm86"),sQuery(id+"F0.wireOp",EDGE,"E17"),sQuery(id+"F0.wireOp",EDGE,"kWYB9zZw-dUfE-JBuI-mU9n-pgfyDcaRUxvO"),sQuery(id+"F0.wireOp",EDGE,"E18"),sQuery(id+"F0.wireOp",EDGE,"vfnI13aN-5aGC-TwJ9-h9OO-FMGUWFeDmuv9"),sQuery(id+"F0.wireOp",EDGE,"E19"),sQuery(id+"F0.wireOp",EDGE,"E20"),sQuery(id+"F0.wireOp",EDGE,"E21"),sQuery(id+"F0.wireOp",EDGE,"E22"),sQuery(id+"F0.wireOp",EDGE,"JsAoEpAL-XQW4-Lyrg-R8HR-OfjOjkPQAlpN"),sQuery(id+"F0.wireOp",EDGE,"QAwi9ICx-SNt3-gAxD-qMH3-k1r5QHOYkTIN"),sQuery(id+"F0.wireOp",EDGE,"bgABXGzA-3ZDr-4HFO-1yYm-MuwqDgoMTBvo"),sQuery(id+"F0.wireOp",EDGE,"wgyuN0RA-UE8u-KT4Y-o13n-P3vcXdWd7IlJ"),sQuery(id+"F0.wireOp",EDGE,"9d0d2092-a8f3-4ebb-af6d-0df3fb4feacb.trimOffspring"),sQuery(id+"F0.wireOp",EDGE,"10fe8deb-c225-4385-8b94-fba867b40c2d.trimOffspring"),sQuery(id+"F0.wireOp",EDGE,"75751931-a2df-4963-a2bf-7204bff7b78a.filletArc"),sQuery(id+"F0.wireOp",EDGE,"e7d6d30a-f864-4f75-85fc-35ceeb29439c.filletArc"),sQuery(id+"F0.wireOp",EDGE,"a49e830f-b283-406d-92e2-e5d81fe63434.filletArc"),sQuery(id+"F0.wireOp",EDGE,"b3d7f47c-b04d-42dd-9b78-bc98ec63f042.filletArc"),sQuery(id+"F0.wireOp",EDGE,"b51091e8-612c-49d7-9d92-63615423fc4d.filletArc"),sQuery(id+"F0.wireOp",EDGE,"E24.filletArc")])],"isStart":false}),makeQuery(id+"F2.opExtrude","SWEPT_FACE",FACE,{"disambiguationData":[OSD([sQuery(id+"F0.wireOp",EDGE,"E14.3")])]})]});
            var Q109;
            Q109=makeQuery(id+"F2.boolean.opBoolean","INTERSECT",EDGE,{"derivedFrom":[makeQuery(id+"F1.opExtrude","CAP_FACE",FACE,{"disambiguationData":[OSD([sQuery(id+"F0.wireOp",EDGE,"E0.0"),sQuery(id+"F0.wireOp",EDGE,"E0.1"),sQuery(id+"F0.wireOp",EDGE,"E0.2"),sQuery(id+"F0.wireOp",EDGE,"E0.3"),sQuery(id+"F0.wireOp",EDGE,"E0.4"),sQuery(id+"F0.wireOp",EDGE,"E0.5"),sQuery(id+"F0.wireOp",EDGE,"E1"),sQuery(id+"F0.wireOp",EDGE,"E2"),sQuery(id+"F0.wireOp",EDGE,"E4"),sQuery(id+"F0.wireOp",EDGE,"E5"),sQuery(id+"F0.wireOp",EDGE,"E6"),sQuery(id+"F0.wireOp",EDGE,"E13.0"),sQuery(id+"F0.wireOp",EDGE,"E0.4"),sQuery(id+"F0.wireOp",EDGE,"E15.0"),sQuery(id+"F0.wireOp",EDGE,"W6VNMVPK-Heu4-H590-lQcW-GhW6zsYcIm86"),sQuery(id+"F0.wireOp",EDGE,"E17"),sQuery(id+"F0.wireOp",EDGE,"kWYB9zZw-dUfE-JBuI-mU9n-pgfyDcaRUxvO"),sQuery(id+"F0.wireOp",EDGE,"E18"),sQuery(id+"F0.wireOp",EDGE,"vfnI13aN-5aGC-TwJ9-h9OO-FMGUWFeDmuv9"),sQuery(id+"F0.wireOp",EDGE,"E19"),sQuery(id+"F0.wireOp",EDGE,"E20"),sQuery(id+"F0.wireOp",EDGE,"E21"),sQuery(id+"F0.wireOp",EDGE,"E22"),sQuery(id+"F0.wireOp",EDGE,"JsAoEpAL-XQW4-Lyrg-R8HR-OfjOjkPQAlpN"),sQuery(id+"F0.wireOp",EDGE,"QAwi9ICx-SNt3-gAxD-qMH3-k1r5QHOYkTIN"),sQuery(id+"F0.wireOp",EDGE,"bgABXGzA-3ZDr-4HFO-1yYm-MuwqDgoMTBvo"),sQuery(id+"F0.wireOp",EDGE,"wgyuN0RA-UE8u-KT4Y-o13n-P3vcXdWd7IlJ"),sQuery(id+"F0.wireOp",EDGE,"9d0d2092-a8f3-4ebb-af6d-0df3fb4feacb.trimOffspring"),sQuery(id+"F0.wireOp",EDGE,"10fe8deb-c225-4385-8b94-fba867b40c2d.trimOffspring"),sQuery(id+"F0.wireOp",EDGE,"75751931-a2df-4963-a2bf-7204bff7b78a.filletArc"),sQuery(id+"F0.wireOp",EDGE,"e7d6d30a-f864-4f75-85fc-35ceeb29439c.filletArc"),sQuery(id+"F0.wireOp",EDGE,"a49e830f-b283-406d-92e2-e5d81fe63434.filletArc"),sQuery(id+"F0.wireOp",EDGE,"b3d7f47c-b04d-42dd-9b78-bc98ec63f042.filletArc"),sQuery(id+"F0.wireOp",EDGE,"b51091e8-612c-49d7-9d92-63615423fc4d.filletArc"),sQuery(id+"F0.wireOp",EDGE,"E24.filletArc")])],"isStart":false}),makeQuery(id+"F2.opExtrude","SWEPT_FACE",FACE,{"disambiguationData":[OSD([sQuery(id+"F0.wireOp",EDGE,"E15.1")])]})]});
            var Q110;
            Q110=makeQuery(id+"F1.opExtrude","CAP_EDGE",EDGE,{"disambiguationData":[OSD([sQuery(id+"F0.wireOp",EDGE,"E2")])],"isStart":false});
            var Q111;
            Q111=makeQuery(id+"F1.opExtrude","CAP_EDGE",EDGE,{"disambiguationData":[OSD([sQuery(id+"F0.wireOp",EDGE,"E18")])],"isStart":true});
            var Q112;
            {var subQ0=sQuery(id+"F0.wireOp",EDGE,"E15.0");var subQ1=sQuery(id+"F0.wireOp",EDGE,"E0.3");var subQ2=sQuery(id+"F0.wireOp",EDGE,"E0.2");Q112=makeQuery(id+"F2.boolean.opBoolean","SPLIT",EDGE,{"disambiguationData":[TD([makeQuery(id+"F1.opExtrude","SWEPT_FACE",FACE,{"disambiguationData":[OSD([subQ1])]})])],"derivedFrom":makeQuery(id+"F1.opExtrude","CAP_EDGE",EDGE,{"disambiguationData":[OSD([subQ2,subQ0])],"isStart":false})});}
            var Q113;
            Q113=makeQuery(id+"F1.opExtrude","CAP_EDGE",EDGE,{"disambiguationData":[OSD([sQuery(id+"F0.wireOp",EDGE,"kWYB9zZw-dUfE-JBuI-mU9n-pgfyDcaRUxvO")])],"isStart":false});
            var Q114;
            Q114=makeQuery(id+"F1.opExtrude","CAP_EDGE",EDGE,{"disambiguationData":[OSD([sQuery(id+"F0.wireOp",EDGE,"E0.5")])],"isStart":true});
            var Q115;
            Q115=makeQuery(id+"F2.opExtrude","SWEPT_EDGE",EDGE,{"disambiguationData":[OSD([sQuery(id+"F0.wireOp",EDGE,"E15.3"),sQuery(id+"F0.wireOp",EDGE,"E15.4")])]});
            var Q116;
            Q116=makeQuery(id+"F2.boolean.opBoolean","INTERSECT",EDGE,{"derivedFrom":[makeQuery(id+"F1.opExtrude","CAP_FACE",FACE,{"disambiguationData":[OSD([sQuery(id+"F0.wireOp",EDGE,"E0.0"),sQuery(id+"F0.wireOp",EDGE,"E0.1"),sQuery(id+"F0.wireOp",EDGE,"E0.2"),sQuery(id+"F0.wireOp",EDGE,"E0.3"),sQuery(id+"F0.wireOp",EDGE,"E0.4"),sQuery(id+"F0.wireOp",EDGE,"E0.5"),sQuery(id+"F0.wireOp",EDGE,"E1"),sQuery(id+"F0.wireOp",EDGE,"E2"),sQuery(id+"F0.wireOp",EDGE,"E4"),sQuery(id+"F0.wireOp",EDGE,"E5"),sQuery(id+"F0.wireOp",EDGE,"E6"),sQuery(id+"F0.wireOp",EDGE,"E13.0"),sQuery(id+"F0.wireOp",EDGE,"E0.4"),sQuery(id+"F0.wireOp",EDGE,"E15.0"),sQuery(id+"F0.wireOp",EDGE,"W6VNMVPK-Heu4-H590-lQcW-GhW6zsYcIm86"),sQuery(id+"F0.wireOp",EDGE,"E17"),sQuery(id+"F0.wireOp",EDGE,"kWYB9zZw-dUfE-JBuI-mU9n-pgfyDcaRUxvO"),sQuery(id+"F0.wireOp",EDGE,"E18"),sQuery(id+"F0.wireOp",EDGE,"vfnI13aN-5aGC-TwJ9-h9OO-FMGUWFeDmuv9"),sQuery(id+"F0.wireOp",EDGE,"E19"),sQuery(id+"F0.wireOp",EDGE,"E20"),sQuery(id+"F0.wireOp",EDGE,"E21"),sQuery(id+"F0.wireOp",EDGE,"E22"),sQuery(id+"F0.wireOp",EDGE,"JsAoEpAL-XQW4-Lyrg-R8HR-OfjOjkPQAlpN"),sQuery(id+"F0.wireOp",EDGE,"QAwi9ICx-SNt3-gAxD-qMH3-k1r5QHOYkTIN"),sQuery(id+"F0.wireOp",EDGE,"bgABXGzA-3ZDr-4HFO-1yYm-MuwqDgoMTBvo"),sQuery(id+"F0.wireOp",EDGE,"wgyuN0RA-UE8u-KT4Y-o13n-P3vcXdWd7IlJ"),sQuery(id+"F0.wireOp",EDGE,"9d0d2092-a8f3-4ebb-af6d-0df3fb4feacb.trimOffspring"),sQuery(id+"F0.wireOp",EDGE,"10fe8deb-c225-4385-8b94-fba867b40c2d.trimOffspring"),sQuery(id+"F0.wireOp",EDGE,"75751931-a2df-4963-a2bf-7204bff7b78a.filletArc"),sQuery(id+"F0.wireOp",EDGE,"e7d6d30a-f864-4f75-85fc-35ceeb29439c.filletArc"),sQuery(id+"F0.wireOp",EDGE,"a49e830f-b283-406d-92e2-e5d81fe63434.filletArc"),sQuery(id+"F0.wireOp",EDGE,"b3d7f47c-b04d-42dd-9b78-bc98ec63f042.filletArc"),sQuery(id+"F0.wireOp",EDGE,"b51091e8-612c-49d7-9d92-63615423fc4d.filletArc"),sQuery(id+"F0.wireOp",EDGE,"E24.filletArc")])],"isStart":false}),makeQuery(id+"F2.opExtrude","SWEPT_FACE",FACE,{"disambiguationData":[OSD([sQuery(id+"F0.wireOp",EDGE,"E14.1")])]})]});
            var Q117;
            Q117=makeQuery(id+"F1.opExtrude","SWEPT_EDGE",EDGE,{"disambiguationData":[OSD([sQuery(id+"F0.wireOp",EDGE,"E17"),sQuery(id+"F0.wireOp",EDGE,"kWYB9zZw-dUfE-JBuI-mU9n-pgfyDcaRUxvO")])]});
            var Q118;
            Q118=makeQuery(id+"F1.opExtrude","SWEPT_FACE",FACE,{"disambiguationData":[OSD([sQuery(id+"F0.wireOp",EDGE,"e7d6d30a-f864-4f75-85fc-35ceeb29439c.filletArc")])]});
            var Q119;
            Q119=makeQuery(id+"F1.opExtrude","SWEPT_FACE",FACE,{"disambiguationData":[OSD([sQuery(id+"F0.wireOp",EDGE,"E21")])]});
            var Q120;
            Q120=makeQuery(id+"F1.opExtrude","CAP_EDGE",EDGE,{"disambiguationData":[OSD([sQuery(id+"F0.wireOp",EDGE,"E20")])],"isStart":false});
            var Q121;
            Q121=makeQuery(id+"F1.opExtrude","SWEPT_EDGE",EDGE,{"disambiguationData":[OSD([sQuery(id+"F0.wireOp",EDGE,"E0.3"),sQuery(id+"F0.wireOp",EDGE,"E0.4")])]});
            var Q122;
            Q122=makeQuery(id+"F1.opExtrude","SWEPT_EDGE",EDGE,{"disambiguationData":[OSD([sQuery(id+"F0.wireOp",EDGE,"kWYB9zZw-dUfE-JBuI-mU9n-pgfyDcaRUxvO"),sQuery(id+"F0.wireOp",EDGE,"E18")])]});
            var Q123;
            Q123=makeQuery(id+"F1.opExtrude","CAP_EDGE",EDGE,{"disambiguationData":[OSD([sQuery(id+"F0.wireOp",EDGE,"W6VNMVPK-Heu4-H590-lQcW-GhW6zsYcIm86")])],"isStart":false});
            var Q124;
            {var subQ0=sQuery(id+"F0.wireOp",EDGE,"E0.3");var subQ1=sQuery(id+"F0.wireOp",EDGE,"E0.4");var subQ2=sQuery(id+"F0.wireOp",EDGE,"E0.4");Q124=makeQuery(id+"F2.boolean.opBoolean","SPLIT",EDGE,{"disambiguationData":[TD([makeQuery(id+"F1.opExtrude","SWEPT_FACE",FACE,{"disambiguationData":[OSD([subQ0])]})])],"derivedFrom":makeQuery(id+"F1.opExtrude","CAP_EDGE",EDGE,{"disambiguationData":[OSD([subQ2,subQ1])],"isStart":false})});}
            var Q125;
            Q125=makeQuery(id+"F2.opExtrude","CAP_EDGE",EDGE,{"disambiguationData":[OSD([sQuery(id+"F0.wireOp",EDGE,"E6")])],"isStart":false});
            var Q126;
            Q126=makeQuery(id+"F1.opExtrude","CAP_EDGE",EDGE,{"disambiguationData":[OSD([sQuery(id+"F0.wireOp",EDGE,"E1")])],"isStart":false});
            var Q127;
            Q127=makeQuery(id+"F1.opExtrude","CAP_EDGE",EDGE,{"disambiguationData":[OSD([sQuery(id+"F0.wireOp",EDGE,"vfnI13aN-5aGC-TwJ9-h9OO-FMGUWFeDmuv9")])],"isStart":false});
            var Q128;
            Q128=makeQuery(id+"F2.boolean.opBoolean","INTERSECT",EDGE,{"derivedFrom":[makeQuery(id+"F1.opExtrude","CAP_FACE",FACE,{"disambiguationData":[OSD([sQuery(id+"F0.wireOp",EDGE,"E0.0"),sQuery(id+"F0.wireOp",EDGE,"E0.1"),sQuery(id+"F0.wireOp",EDGE,"E0.2"),sQuery(id+"F0.wireOp",EDGE,"E0.3"),sQuery(id+"F0.wireOp",EDGE,"E0.4"),sQuery(id+"F0.wireOp",EDGE,"E0.5"),sQuery(id+"F0.wireOp",EDGE,"E1"),sQuery(id+"F0.wireOp",EDGE,"E2"),sQuery(id+"F0.wireOp",EDGE,"E4"),sQuery(id+"F0.wireOp",EDGE,"E5"),sQuery(id+"F0.wireOp",EDGE,"E6"),sQuery(id+"F0.wireOp",EDGE,"E13.0"),sQuery(id+"F0.wireOp",EDGE,"E0.4"),sQuery(id+"F0.wireOp",EDGE,"E15.0"),sQuery(id+"F0.wireOp",EDGE,"W6VNMVPK-Heu4-H590-lQcW-GhW6zsYcIm86"),sQuery(id+"F0.wireOp",EDGE,"E17"),sQuery(id+"F0.wireOp",EDGE,"kWYB9zZw-dUfE-JBuI-mU9n-pgfyDcaRUxvO"),sQuery(id+"F0.wireOp",EDGE,"E18"),sQuery(id+"F0.wireOp",EDGE,"vfnI13aN-5aGC-TwJ9-h9OO-FMGUWFeDmuv9"),sQuery(id+"F0.wireOp",EDGE,"E19"),sQuery(id+"F0.wireOp",EDGE,"E20"),sQuery(id+"F0.wireOp",EDGE,"E21"),sQuery(id+"F0.wireOp",EDGE,"E22"),sQuery(id+"F0.wireOp",EDGE,"JsAoEpAL-XQW4-Lyrg-R8HR-OfjOjkPQAlpN"),sQuery(id+"F0.wireOp",EDGE,"QAwi9ICx-SNt3-gAxD-qMH3-k1r5QHOYkTIN"),sQuery(id+"F0.wireOp",EDGE,"bgABXGzA-3ZDr-4HFO-1yYm-MuwqDgoMTBvo"),sQuery(id+"F0.wireOp",EDGE,"wgyuN0RA-UE8u-KT4Y-o13n-P3vcXdWd7IlJ"),sQuery(id+"F0.wireOp",EDGE,"9d0d2092-a8f3-4ebb-af6d-0df3fb4feacb.trimOffspring"),sQuery(id+"F0.wireOp",EDGE,"10fe8deb-c225-4385-8b94-fba867b40c2d.trimOffspring"),sQuery(id+"F0.wireOp",EDGE,"75751931-a2df-4963-a2bf-7204bff7b78a.filletArc"),sQuery(id+"F0.wireOp",EDGE,"e7d6d30a-f864-4f75-85fc-35ceeb29439c.filletArc"),sQuery(id+"F0.wireOp",EDGE,"a49e830f-b283-406d-92e2-e5d81fe63434.filletArc"),sQuery(id+"F0.wireOp",EDGE,"b3d7f47c-b04d-42dd-9b78-bc98ec63f042.filletArc"),sQuery(id+"F0.wireOp",EDGE,"b51091e8-612c-49d7-9d92-63615423fc4d.filletArc"),sQuery(id+"F0.wireOp",EDGE,"E24.filletArc")])],"isStart":false}),makeQuery(id+"F2.opExtrude","SWEPT_FACE",FACE,{"disambiguationData":[OSD([sQuery(id+"F0.wireOp",EDGE,"E14.5")])]})]});
            var Q129;
            Q129=makeQuery(id+"F1.opExtrude","SWEPT_FACE",FACE,{"disambiguationData":[OSD([sQuery(id+"F0.wireOp",EDGE,"E22")])]});
            var Q130;
            Q130=makeQuery(id+"F1.opExtrude","CAP_EDGE",EDGE,{"disambiguationData":[OSD([sQuery(id+"F0.wireOp",EDGE,"E19")])],"isStart":false});
            var Q131;
            Q131=makeQuery(id+"F1.opExtrude","SWEPT_EDGE",EDGE,{"disambiguationData":[OSD([sQuery(id+"F0.wireOp",EDGE,"W6VNMVPK-Heu4-H590-lQcW-GhW6zsYcIm86"),sQuery(id+"F0.wireOp",EDGE,"9d0d2092-a8f3-4ebb-af6d-0df3fb4feacb.trimOffspring")])]});
            var Q132;
            Q132=makeQuery(id+"F1.opExtrude","SWEPT_FACE",FACE,{"disambiguationData":[OSD([sQuery(id+"F0.wireOp",EDGE,"9d0d2092-a8f3-4ebb-af6d-0df3fb4feacb.trimOffspring")])]});
            var Q133;
            Q133=makeQuery(id+"F1.opExtrude","CAP_EDGE",EDGE,{"disambiguationData":[OSD([sQuery(id+"F0.wireOp",EDGE,"E2")])],"isStart":true});
            var Q134;
            Q134=makeQuery(id+"F1.opExtrude","SWEPT_FACE",FACE,{"disambiguationData":[OSD([sQuery(id+"F0.wireOp",EDGE,"10fe8deb-c225-4385-8b94-fba867b40c2d.trimOffspring")])]});
            var Q135;
            Q135=makeQuery(id+"F1.opExtrude","CAP_EDGE",EDGE,{"disambiguationData":[OSD([sQuery(id+"F0.wireOp",EDGE,"E19")])],"isStart":true});
            var Q136;
            Q136=makeQuery(id+"F1.opExtrude","CAP_EDGE",EDGE,{"disambiguationData":[OSD([sQuery(id+"F0.wireOp",EDGE,"9d0d2092-a8f3-4ebb-af6d-0df3fb4feacb.trimOffspring")])],"isStart":false});
            var Q137;
            Q137=makeQuery(id+"F1.opExtrude","SWEPT_FACE",FACE,{"disambiguationData":[OSD([sQuery(id+"F0.wireOp",EDGE,"75751931-a2df-4963-a2bf-7204bff7b78a.filletArc")])]});
            var Q138;
            Q138=makeQuery(id+"F1.opExtrude","CAP_EDGE",EDGE,{"disambiguationData":[OSD([sQuery(id+"F0.wireOp",EDGE,"E20")])],"isStart":true});
            var Q139;
            Q139=makeQuery(id+"F1.opExtrude","CAP_EDGE",EDGE,{"disambiguationData":[OSD([sQuery(id+"F0.wireOp",EDGE,"e7d6d30a-f864-4f75-85fc-35ceeb29439c.filletArc")])],"isStart":false});
            var Q140;
            Q140=makeQuery(id+"F1.opExtrude","CAP_EDGE",EDGE,{"disambiguationData":[OSD([sQuery(id+"F0.wireOp",EDGE,"E22")])],"isStart":false});
            var Q141;
            Q141=makeQuery(id+"F1.opExtrude","CAP_EDGE",EDGE,{"disambiguationData":[OSD([sQuery(id+"F0.wireOp",EDGE,"E1")])],"isStart":true});
            var Q142;
            Q142=makeQuery(id+"F1.opExtrude","CAP_EDGE",EDGE,{"disambiguationData":[OSD([sQuery(id+"F0.wireOp",EDGE,"75751931-a2df-4963-a2bf-7204bff7b78a.filletArc")])],"isStart":false});
            var Q143;
            Q143=makeQuery(id+"F1.opExtrude","CAP_EDGE",EDGE,{"disambiguationData":[OSD([sQuery(id+"F0.wireOp",EDGE,"JsAoEpAL-XQW4-Lyrg-R8HR-OfjOjkPQAlpN"),sQuery(id+"F0.wireOp",EDGE,"bgABXGzA-3ZDr-4HFO-1yYm-MuwqDgoMTBvo")])],"isStart":false});
            var Q144;
            Q144=makeQuery(id+"F1.opExtrude","SWEPT_FACE",FACE,{"disambiguationData":[OSD([sQuery(id+"F0.wireOp",EDGE,"a49e830f-b283-406d-92e2-e5d81fe63434.filletArc")])]});
            var Q145;
            Q145=makeQuery(id+"F1.opExtrude","CAP_EDGE",EDGE,{"disambiguationData":[OSD([sQuery(id+"F0.wireOp",EDGE,"vfnI13aN-5aGC-TwJ9-h9OO-FMGUWFeDmuv9")])],"isStart":true});
            var Q146;
            Q146=makeQuery(id+"F1.opExtrude","CAP_EDGE",EDGE,{"disambiguationData":[OSD([sQuery(id+"F0.wireOp",EDGE,"E21")])],"isStart":false});
            var Q147;
            Q147=makeQuery(id+"F1.opExtrude","SWEPT_EDGE",EDGE,{"disambiguationData":[OSD([sQuery(id+"F0.wireOp",EDGE,"9d0d2092-a8f3-4ebb-af6d-0df3fb4feacb.trimOffspring"),sQuery(id+"F0.wireOp",EDGE,"75751931-a2df-4963-a2bf-7204bff7b78a.filletArc")])]});
            var Q148;
            Q148=makeQuery(id+"F1.opExtrude","SWEPT_FACE",FACE,{"disambiguationData":[OSD([sQuery(id+"F0.wireOp",EDGE,"E24.filletArc")])]});
            var Q149;
            Q149=makeQuery(id+"F1.opExtrude","SWEPT_FACE",FACE,{"disambiguationData":[OSD([sQuery(id+"F0.wireOp",EDGE,"b3d7f47c-b04d-42dd-9b78-bc98ec63f042.filletArc")])]});
            var Q150;
            Q150=makeQuery(id+"F1.opExtrude","CAP_EDGE",EDGE,{"disambiguationData":[OSD([sQuery(id+"F0.wireOp",EDGE,"E6")])],"isStart":true});
            var Q151;
            Q151=makeQuery(id+"F1.opExtrude","SWEPT_FACE",FACE,{"disambiguationData":[OSD([sQuery(id+"F0.wireOp",EDGE,"QAwi9ICx-SNt3-gAxD-qMH3-k1r5QHOYkTIN")])]});
            var Q152;
            Q152=makeQuery(id+"F1.opExtrude","CAP_EDGE",EDGE,{"disambiguationData":[OSD([sQuery(id+"F0.wireOp",EDGE,"E4")])],"isStart":true});
            var Q153;
            Q153=makeQuery(id+"F1.opExtrude","SWEPT_EDGE",EDGE,{"disambiguationData":[OSD([sQuery(id+"F0.wireOp",EDGE,"E21"),sQuery(id+"F0.wireOp",EDGE,"75751931-a2df-4963-a2bf-7204bff7b78a.filletArc")])]});
            var Q154;
            Q154=makeQuery(id+"F1.opExtrude","SWEPT_FACE",FACE,{"disambiguationData":[OSD([sQuery(id+"F0.wireOp",EDGE,"vfnI13aN-5aGC-TwJ9-h9OO-FMGUWFeDmuv9")])]});
            var Q155;
            Q155=makeQuery(id+"F1.opExtrude","SWEPT_EDGE",EDGE,{"disambiguationData":[OSD([sQuery(id+"F0.wireOp",EDGE,"E21"),sQuery(id+"F0.wireOp",EDGE,"e7d6d30a-f864-4f75-85fc-35ceeb29439c.filletArc")])]});
            var Q156;
            Q156=makeQuery(id+"F1.opExtrude","SWEPT_FACE",FACE,{"disambiguationData":[OSD([sQuery(id+"F0.wireOp",EDGE,"JsAoEpAL-XQW4-Lyrg-R8HR-OfjOjkPQAlpN"),sQuery(id+"F0.wireOp",EDGE,"bgABXGzA-3ZDr-4HFO-1yYm-MuwqDgoMTBvo")])]});
            var Q157;
            Q157=makeQuery(id+"F1.opExtrude","CAP_EDGE",EDGE,{"disambiguationData":[OSD([sQuery(id+"F0.wireOp",EDGE,"E5")])],"isStart":true});
            var Q158;
            Q158=makeQuery(id+"F1.opExtrude","SWEPT_EDGE",EDGE,{"disambiguationData":[OSD([sQuery(id+"F0.wireOp",EDGE,"JsAoEpAL-XQW4-Lyrg-R8HR-OfjOjkPQAlpN"),sQuery(id+"F0.wireOp",EDGE,"a49e830f-b283-406d-92e2-e5d81fe63434.filletArc")])]});
            var Q159;
            Q159=makeQuery(id+"F1.opExtrude","SWEPT_EDGE",EDGE,{"disambiguationData":[OSD([sQuery(id+"F0.wireOp",EDGE,"E18"),sQuery(id+"F0.wireOp",EDGE,"vfnI13aN-5aGC-TwJ9-h9OO-FMGUWFeDmuv9")])]});
            var Q160;
            Q160=makeQuery(id+"F1.opExtrude","CAP_EDGE",EDGE,{"disambiguationData":[OSD([sQuery(id+"F0.wireOp",EDGE,"E22")])],"isStart":true});
            var Q161;
            Q161=makeQuery(id+"F1.opExtrude","CAP_EDGE",EDGE,{"disambiguationData":[OSD([sQuery(id+"F0.wireOp",EDGE,"E24.filletArc")])],"isStart":false});
            var Q162;
            Q162=makeQuery(id+"F1.opExtrude","SWEPT_EDGE",EDGE,{"disambiguationData":[OSD([sQuery(id+"F0.wireOp",EDGE,"E22"),sQuery(id+"F0.wireOp",EDGE,"b3d7f47c-b04d-42dd-9b78-bc98ec63f042.filletArc")])]});
            var Q163;
            Q163=makeQuery(id+"F1.opExtrude","SWEPT_EDGE",EDGE,{"disambiguationData":[OSD([sQuery(id+"F0.wireOp",EDGE,"E22"),sQuery(id+"F0.wireOp",EDGE,"E24.filletArc")])]});
            var Q164;
            Q164=makeQuery(id+"F1.opExtrude","SWEPT_EDGE",EDGE,{"disambiguationData":[OSD([sQuery(id+"F0.wireOp",EDGE,"QAwi9ICx-SNt3-gAxD-qMH3-k1r5QHOYkTIN"),sQuery(id+"F0.wireOp",EDGE,"e7d6d30a-f864-4f75-85fc-35ceeb29439c.filletArc")])]});
            var Q165;
            Q165=makeQuery(id+"F1.opExtrude","SWEPT_FACE",FACE,{"disambiguationData":[OSD([sQuery(id+"F0.wireOp",EDGE,"wgyuN0RA-UE8u-KT4Y-o13n-P3vcXdWd7IlJ")])]});
            var Q166;
            Q166=makeQuery(id+"F1.opExtrude","SWEPT_EDGE",EDGE,{"disambiguationData":[OSD([sQuery(id+"F0.wireOp",EDGE,"10fe8deb-c225-4385-8b94-fba867b40c2d.trimOffspring"),sQuery(id+"F0.wireOp",EDGE,"E24.filletArc")])]});
            var Q167;
            Q167=makeQuery(id+"F1.opExtrude","CAP_EDGE",EDGE,{"disambiguationData":[OSD([sQuery(id+"F0.wireOp",EDGE,"b3d7f47c-b04d-42dd-9b78-bc98ec63f042.filletArc")])],"isStart":false});
            var Q168;
            Q168=makeQuery(id+"F1.opExtrude","SWEPT_EDGE",EDGE,{"disambiguationData":[OSD([sQuery(id+"F0.wireOp",EDGE,"QAwi9ICx-SNt3-gAxD-qMH3-k1r5QHOYkTIN"),sQuery(id+"F0.wireOp",EDGE,"a49e830f-b283-406d-92e2-e5d81fe63434.filletArc")])]});
            var Q169;
            Q169=makeQuery(id+"F1.opExtrude","CAP_EDGE",EDGE,{"disambiguationData":[OSD([sQuery(id+"F0.wireOp",EDGE,"QAwi9ICx-SNt3-gAxD-qMH3-k1r5QHOYkTIN")])],"isStart":false});
            var Q170;
            Q170=makeQuery(id+"F1.opExtrude","SWEPT_FACE",FACE,{"disambiguationData":[OSD([sQuery(id+"F0.wireOp",EDGE,"b51091e8-612c-49d7-9d92-63615423fc4d.filletArc")])]});
            var Q171;
            Q171=makeQuery(id+"F1.opExtrude","SWEPT_EDGE",EDGE,{"disambiguationData":[OSD([sQuery(id+"F0.wireOp",EDGE,"wgyuN0RA-UE8u-KT4Y-o13n-P3vcXdWd7IlJ"),sQuery(id+"F0.wireOp",EDGE,"b3d7f47c-b04d-42dd-9b78-bc98ec63f042.filletArc")])]});
            var Q172;
            Q172=makeQuery(id+"F1.opExtrude","CAP_EDGE",EDGE,{"disambiguationData":[OSD([sQuery(id+"F0.wireOp",EDGE,"JsAoEpAL-XQW4-Lyrg-R8HR-OfjOjkPQAlpN"),sQuery(id+"F0.wireOp",EDGE,"bgABXGzA-3ZDr-4HFO-1yYm-MuwqDgoMTBvo")])],"isStart":true});
            var Q173;
            Q173=makeQuery(id+"F1.opExtrude","SWEPT_EDGE",EDGE,{"disambiguationData":[OSD([sQuery(id+"F0.wireOp",EDGE,"vfnI13aN-5aGC-TwJ9-h9OO-FMGUWFeDmuv9"),sQuery(id+"F0.wireOp",EDGE,"10fe8deb-c225-4385-8b94-fba867b40c2d.trimOffspring")])]});
            var Q174;
            Q174=makeQuery(id+"F1.opExtrude","CAP_EDGE",EDGE,{"disambiguationData":[OSD([sQuery(id+"F0.wireOp",EDGE,"E24.filletArc")])],"isStart":true});
            var Q175;
            Q175=makeQuery(id+"F1.opExtrude","CAP_EDGE",EDGE,{"disambiguationData":[OSD([sQuery(id+"F0.wireOp",EDGE,"10fe8deb-c225-4385-8b94-fba867b40c2d.trimOffspring")])],"isStart":true});
            var Q176;
            Q176=makeQuery(id+"F1.opExtrude","CAP_EDGE",EDGE,{"disambiguationData":[OSD([sQuery(id+"F0.wireOp",EDGE,"9d0d2092-a8f3-4ebb-af6d-0df3fb4feacb.trimOffspring")])],"isStart":true});
            var Q177;
            Q177=makeQuery(id+"F1.opExtrude","CAP_EDGE",EDGE,{"disambiguationData":[OSD([sQuery(id+"F0.wireOp",EDGE,"10fe8deb-c225-4385-8b94-fba867b40c2d.trimOffspring")])],"isStart":false});
            var Q178;
            Q178=makeQuery(id+"F1.opExtrude","CAP_EDGE",EDGE,{"disambiguationData":[OSD([sQuery(id+"F0.wireOp",EDGE,"a49e830f-b283-406d-92e2-e5d81fe63434.filletArc")])],"isStart":false});
            var Q179;
            Q179=makeQuery(id+"F1.opExtrude","SWEPT_EDGE",EDGE,{"disambiguationData":[OSD([sQuery(id+"F0.wireOp",EDGE,"wgyuN0RA-UE8u-KT4Y-o13n-P3vcXdWd7IlJ"),sQuery(id+"F0.wireOp",EDGE,"b51091e8-612c-49d7-9d92-63615423fc4d.filletArc")])]});
            var Q180;
            Q180=makeQuery(id+"F1.opExtrude","CAP_EDGE",EDGE,{"disambiguationData":[OSD([sQuery(id+"F0.wireOp",EDGE,"E21")])],"isStart":true});
            var Q181;
            Q181=makeQuery(id+"F1.opExtrude","CAP_EDGE",EDGE,{"disambiguationData":[OSD([sQuery(id+"F0.wireOp",EDGE,"75751931-a2df-4963-a2bf-7204bff7b78a.filletArc")])],"isStart":true});
            var Q182;
            Q182=makeQuery(id+"F1.opExtrude","CAP_EDGE",EDGE,{"disambiguationData":[OSD([sQuery(id+"F0.wireOp",EDGE,"wgyuN0RA-UE8u-KT4Y-o13n-P3vcXdWd7IlJ")])],"isStart":false});
            var Q183;
            Q183=makeQuery(id+"F1.opExtrude","CAP_EDGE",EDGE,{"disambiguationData":[OSD([sQuery(id+"F0.wireOp",EDGE,"e7d6d30a-f864-4f75-85fc-35ceeb29439c.filletArc")])],"isStart":true});
            var Q184;
            Q184=makeQuery(id+"F1.opExtrude","SWEPT_EDGE",EDGE,{"disambiguationData":[OSD([sQuery(id+"F0.wireOp",EDGE,"bgABXGzA-3ZDr-4HFO-1yYm-MuwqDgoMTBvo"),sQuery(id+"F0.wireOp",EDGE,"b51091e8-612c-49d7-9d92-63615423fc4d.filletArc")])]});
            var Q185;
            Q185=makeQuery(id+"F1.opExtrude","CAP_EDGE",EDGE,{"disambiguationData":[OSD([sQuery(id+"F0.wireOp",EDGE,"b51091e8-612c-49d7-9d92-63615423fc4d.filletArc")])],"isStart":false});
            var Q186;
            Q186=makeQuery(id+"F1.opExtrude","CAP_EDGE",EDGE,{"disambiguationData":[OSD([sQuery(id+"F0.wireOp",EDGE,"a49e830f-b283-406d-92e2-e5d81fe63434.filletArc")])],"isStart":true});
            var Q187;
            Q187=makeQuery(id+"F1.opExtrude","CAP_EDGE",EDGE,{"disambiguationData":[OSD([sQuery(id+"F0.wireOp",EDGE,"QAwi9ICx-SNt3-gAxD-qMH3-k1r5QHOYkTIN")])],"isStart":true});
            var Q188;
            Q188=makeQuery(id+"F1.opExtrude","CAP_EDGE",EDGE,{"disambiguationData":[OSD([sQuery(id+"F0.wireOp",EDGE,"b3d7f47c-b04d-42dd-9b78-bc98ec63f042.filletArc")])],"isStart":true});
            var Q189;
            Q189=makeQuery(id+"F1.opExtrude","CAP_EDGE",EDGE,{"disambiguationData":[OSD([sQuery(id+"F0.wireOp",EDGE,"wgyuN0RA-UE8u-KT4Y-o13n-P3vcXdWd7IlJ")])],"isStart":true});
            var Q190;
            Q190=makeQuery(id+"F1.opExtrude","CAP_EDGE",EDGE,{"disambiguationData":[OSD([sQuery(id+"F0.wireOp",EDGE,"b51091e8-612c-49d7-9d92-63615423fc4d.filletArc")])],"isStart":true});
            fillet(context, id + "F3", {"entities" : qUnion([Q0, Q1, Q2, Q3, Q4, Q5, Q6, Q7, Q8, Q9, Q10, Q11, Q12, Q13, Q14, Q15, Q16, Q17, Q18, Q19, Q20, Q21, Q22, Q23, Q24, Q25, Q26, Q27, Q28, Q29, Q30, Q31, Q32, Q33, Q34, Q35, Q36, Q37, Q38, Q39, Q40, Q41, Q42, Q43, Q44, Q45, Q46, Q47, Q48, Q49, Q50, Q51, Q52, Q53, Q54, Q55, Q56, Q57, Q58, Q59, Q60, Q61, Q62, Q63, Q64, Q65, Q66, Q67, Q68, Q69, Q70, Q71, Q72, Q73, Q74, Q75, Q76, Q77, Q78, Q79, Q80, Q81, Q82, Q83, Q84, Q85, Q86, Q87, Q88, Q89, Q90, Q91, Q92, Q93, Q94, Q95, Q96, Q97, Q98, Q99, Q100, Q101, Q102, Q103, Q104, Q105, Q106, Q107, Q108, Q109, Q110, Q111, Q112, Q113, Q114, Q115, Q116, Q117, Q118, Q119, Q120, Q121, Q122, Q123, Q124, Q125, Q126, Q127, Q128, Q129, Q130, Q131, Q132, Q133, Q134, Q135, Q136, Q137, Q138, Q139, Q140, Q141, Q142, Q143, Q144, Q145, Q146, Q147, Q148, Q149, Q150, Q151, Q152, Q153, Q154, Q155, Q156, Q157, Q158, Q159, Q160, Q161, Q162, Q163, Q164, Q165, Q166, Q167, Q168, Q169, Q170, Q171, Q172, Q173, Q174, Q175, Q176, Q177, Q178, Q179, Q180, Q181, Q182, Q183, Q184, Q185, Q186, Q187, Q188, Q189, Q190]), "radius" : 0.5 * mm, "tangentPropagation" : true, "allowEdgeOverflow" : false});
        }
        {
            var Q0;
            Q0=makeQuery(id+"F0.imprint","IMPRINT",FACE,{"disambiguationData":[TD([[makeQuery(id+"F0.imprint","IMPRINT",EDGE,{"derivedFrom":sQuery(id+"F0.wireOp",EDGE,"E0.0")}),-1.0]])]});
            var sketch = newSketch(context, id + "F4", { "sketchPlane" : qUnion([Q0])});
            skArc(sketch, "E56", {"start": v(13.53, 43.26) * mm, "mid": v(-0.56, 68.14) * mm, "end": v(-13.77, 42.78) * mm});
            skArc(sketch, "E57", {"start": v(-44.07, 5.37) * mm, "mid": v(-63.46, -0.2) * mm, "end": v(-43.9, -5.11) * mm});
            skArc(sketch, "E58", {"start": v(13.16, -42.32) * mm, "mid": v(38.65, -54.47) * mm, "end": v(29.87, -27.63) * mm});
            skArc(sketch, "E59", {"start": v(13.53, 43.26) * mm, "mid": v(-0.14, 43.9) * mm, "end": v(-13.77, 42.78) * mm});
            skArc(sketch, "E60", {"start": v(-43.9, -5.11) * mm, "mid": v(-43.07, 0.15) * mm, "end": v(-44.07, 5.37) * mm});
            skArc(sketch, "E61", {"start": v(13.16, -42.32) * mm, "mid": v(21.55, -35.01) * mm, "end": v(29.87, -27.63) * mm});
            skSolve(sketch);
        }
        {
            var Q0;
            {var subQ0=makeQuery(id+"F0.imprint","IMPRINT",EDGE,{"derivedFrom":sQuery(id+"F0.wireOp",EDGE,"E0.2")});Q0=makeQuery(id+"F4.imprint","IMPRINT",FACE,{"disambiguationData":[TD([[makeQuery(id+"F4.imprint","IMPRINT",EDGE,{"derivedFrom":subQ0}),1.0]])]});}
            var Q1;
            {var subQ0=sQuery(id+"F4.wireOp",EDGE,"E59");Q1=makeQuery(id+"F4.imprint","IMPRINT",FACE,{"disambiguationData":[TD([[makeQuery(id+"F4.imprint","IMPRINT",EDGE,{"derivedFrom":subQ0}),-1.0]])]});}
            var Q2;
            {var subQ0=sQuery(id+"F4.wireOp",EDGE,"E56");var subQ1=makeQuery(id+"F0.imprint","IMPRINT",EDGE,{"derivedFrom":sQuery(id+"F0.wireOp",EDGE,"E47.filletArc")});var subQ2=makeQuery(id+"F4.imprint","INTERSECT",VERTEX,{"disambiguationData":[OD(0.0)],"derivedFrom":[subQ1,subQ0]});Q2=makeQuery(id+"F4.imprint","IMPRINT",FACE,{"disambiguationData":[TD([[makeQuery(id+"F4.imprint","IMPRINT",EDGE,{"disambiguationData":[TD([[subQ2,-1.0]])],"derivedFrom":subQ0}),1.0]])]});}
            var Q3;
            Q3=makeQuery(id+"F4.imprint","IMPRINT",FACE,{"disambiguationData":[TD([[makeQuery(id+"F4.imprint","IMPRINT",EDGE,{"derivedFrom":sQuery(id+"F4.wireOp",EDGE,"E57")}),1.0]])]});
            var Q4;
            {var subQ1=makeQuery(id+"F0.imprint","IMPRINT",EDGE,{"derivedFrom":sQuery(id+"F0.wireOp",EDGE,"E0.2")});Q4=makeQuery(id+"F4.imprint","IMPRINT",FACE,{"disambiguationData":[TD([[makeQuery(id+"F4.imprint","IMPRINT",EDGE,{"derivedFrom":subQ1}),-1.0]])]});}
            var Q5;
            {var subQ0=sQuery(id+"F4.wireOp",EDGE,"E61");var subQ1=sQuery(id+"F4.wireOp",EDGE,"E58");var subQ2=makeQuery(id+"F4.imprint","INTERSECT",VERTEX,{"disambiguationData":[OD(1.0)],"derivedFrom":[subQ1,subQ0]});Q5=makeQuery(id+"F4.imprint","IMPRINT",FACE,{"disambiguationData":[TD([[makeQuery(id+"F4.imprint","IMPRINT",EDGE,{"disambiguationData":[TD([[subQ2,1.0]])],"derivedFrom":subQ1}),1.0]])]});}
            extrude(context, id + "F5", {"entities" : qUnion([Q0, Q1, Q2, Q3, Q4, Q5]), "operationType" : NewBodyOperationType.ADD, "depth" : 0.3 * mm});
        }
    });
